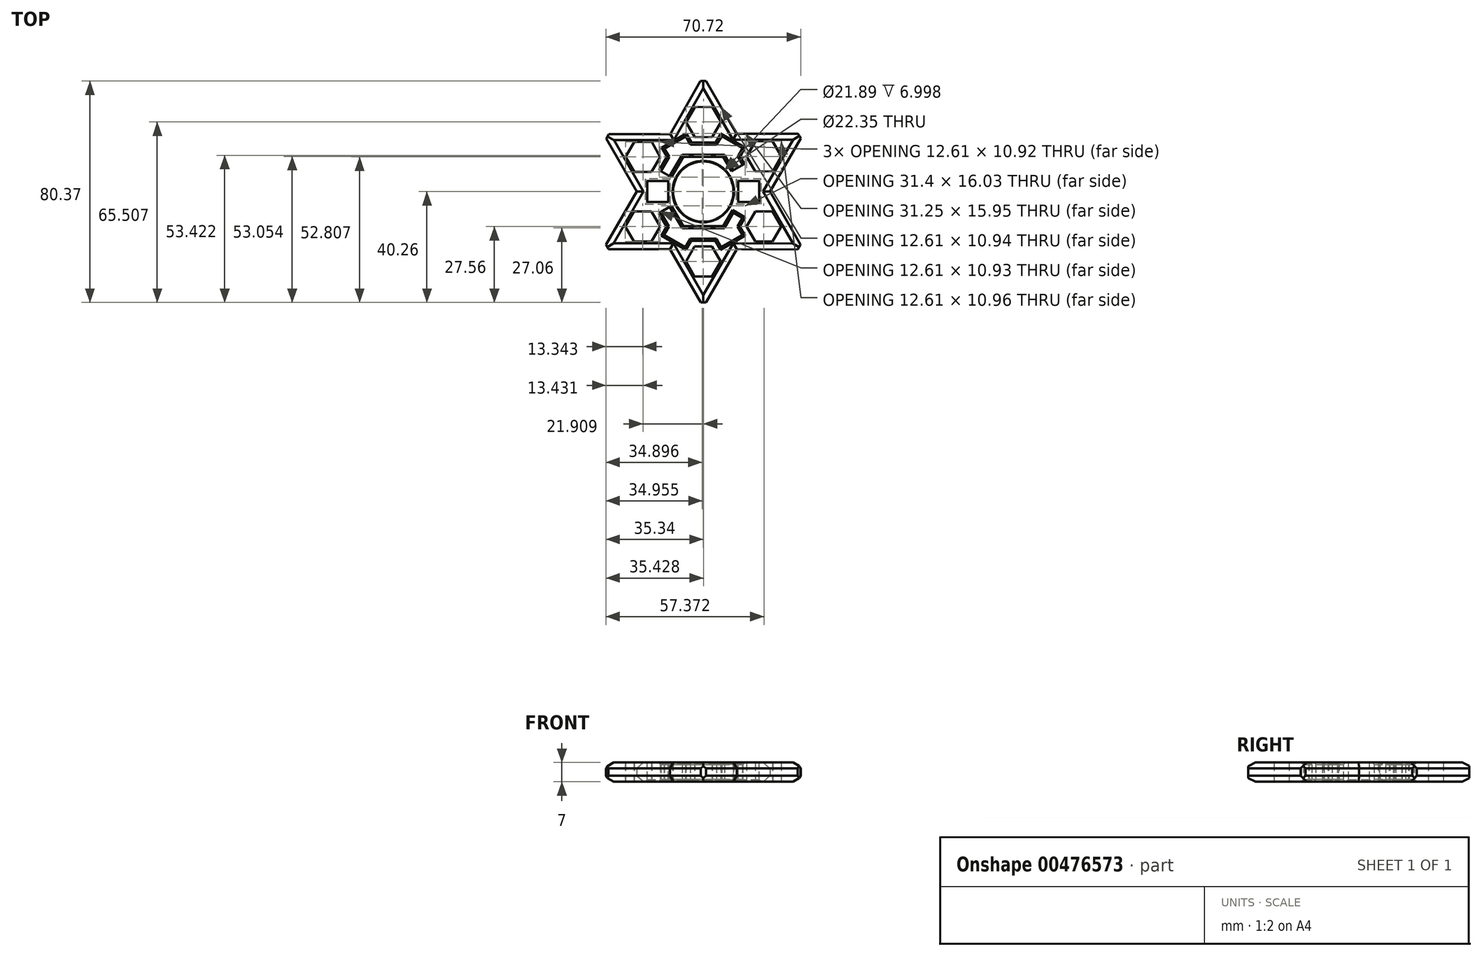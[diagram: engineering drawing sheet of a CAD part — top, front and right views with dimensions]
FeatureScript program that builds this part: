
annotation { "Feature Type Name" : "Feature", "Feature Type Description" : "" }
export const myFeature = defineFeature(function(context is Context, id is Id, definition is map)
    precondition{}
    {
        {
            var Q0;
            Q0=qCreatedBy(makeId("Top.planeOp"),FACE);
            var sketch = newSketch(context, id + "F0", { "sketchPlane" : qUnion([Q0])});
            skCircle(sketch, "E0", {"center": v(0, 0) * mm, "radius": 10.95 * mm});
            skCircle(sketch, "E1.cCircle", {"center": v(0, 0) * mm, "radius": 12.7 * mm, "construction": true});
            skLineSegment(sketch, "E1.0", {"start": v(-7.33, 12.7) * mm, "end": v(7.33, 12.7) * mm});
            skLineSegment(sketch, "E1.1", {"start": v(7.33, 12.7) * mm, "end": v(14.66, 0) * mm});
            skLineSegment(sketch, "E1.2", {"start": v(14.66, 0) * mm, "end": v(7.33, -12.7) * mm});
            skLineSegment(sketch, "E1.3", {"start": v(7.33, -12.7) * mm, "end": v(-7.33, -12.7) * mm});
            skLineSegment(sketch, "E1.4", {"start": v(-7.33, -12.7) * mm, "end": v(-14.66, 0) * mm});
            skLineSegment(sketch, "E1.5", {"start": v(-14.66, 0) * mm, "end": v(-7.33, 12.7) * mm});
            skPoint(sketch, "E1.0.midPoint", {"position": v(0, 12.7) * mm});
            skPoint(sketch, "E2.endSnap0", {"position": v(0, -12.7) * mm});
            skCircle(sketch, "E3.cCircle", {"center": v(0.09, 25.25) * mm, "radius": 5.46 * mm, "construction": true});
            skLineSegment(sketch, "E3.0", {"start": v(3.26, 19.8) * mm, "end": v(-3.05, 19.78) * mm});
            skLineSegment(sketch, "E3.1", {"start": v(-3.05, 19.78) * mm, "end": v(-6.22, 25.23) * mm});
            skLineSegment(sketch, "E3.2", {"start": v(-6.22, 25.23) * mm, "end": v(-3.08, 30.7) * mm});
            skLineSegment(sketch, "E3.3", {"start": v(-3.08, 30.7) * mm, "end": v(3.22, 30.72) * mm});
            skLineSegment(sketch, "E3.4", {"start": v(3.22, 30.72) * mm, "end": v(6.4, 25.27) * mm});
            skLineSegment(sketch, "E3.5", {"start": v(6.4, 25.27) * mm, "end": v(3.26, 19.8) * mm});
            skPoint(sketch, "E3.0.midPoint", {"position": v(0.1, 19.79) * mm});
            skCircle(sketch, "E4.cCircle", {"center": v(22.03, 12.8) * mm, "radius": 5.46 * mm, "construction": true});
            skLineSegment(sketch, "E4.0", {"start": v(18.92, 7.31) * mm, "end": v(15.73, 12.75) * mm});
            skLineSegment(sketch, "E4.1", {"start": v(15.73, 12.75) * mm, "end": v(18.84, 18.23) * mm});
            skLineSegment(sketch, "E4.2", {"start": v(18.84, 18.23) * mm, "end": v(25.15, 18.28) * mm});
            skLineSegment(sketch, "E4.3", {"start": v(25.15, 18.28) * mm, "end": v(28.34, 12.83) * mm});
            skLineSegment(sketch, "E4.4", {"start": v(28.34, 12.83) * mm, "end": v(25.22, 7.35) * mm});
            skLineSegment(sketch, "E4.5", {"start": v(25.22, 7.35) * mm, "end": v(18.92, 7.31) * mm});
            skPoint(sketch, "E4.0.midPoint", {"position": v(17.32, 10.03) * mm});
            skCircle(sketch, "E5.cCircle", {"center": v(22, -12.7) * mm, "radius": 5.46 * mm, "construction": true});
            skLineSegment(sketch, "E5.0", {"start": v(15.7, -12.7) * mm, "end": v(18.84, -7.24) * mm});
            skLineSegment(sketch, "E5.1", {"start": v(18.84, -7.24) * mm, "end": v(25.15, -7.24) * mm});
            skLineSegment(sketch, "E5.2", {"start": v(25.15, -7.24) * mm, "end": v(28.3, -12.7) * mm});
            skLineSegment(sketch, "E5.3", {"start": v(28.3, -12.7) * mm, "end": v(25.15, -18.16) * mm});
            skLineSegment(sketch, "E5.4", {"start": v(25.15, -18.16) * mm, "end": v(18.85, -18.16) * mm});
            skLineSegment(sketch, "E5.5", {"start": v(18.85, -18.16) * mm, "end": v(15.7, -12.7) * mm});
            skPoint(sketch, "E5.0.midPoint", {"position": v(17.27, -9.97) * mm});
            skCircle(sketch, "E6.cCircle", {"center": v(0, -25.4) * mm, "radius": 5.46 * mm, "construction": true});
            skLineSegment(sketch, "E6.0", {"start": v(-3.15, -19.94) * mm, "end": v(3.15, -19.94) * mm});
            skLineSegment(sketch, "E6.1", {"start": v(3.15, -19.94) * mm, "end": v(6.3, -25.4) * mm});
            skLineSegment(sketch, "E6.2", {"start": v(6.3, -25.4) * mm, "end": v(3.15, -30.86) * mm});
            skLineSegment(sketch, "E6.3", {"start": v(3.15, -30.86) * mm, "end": v(-3.15, -30.86) * mm});
            skLineSegment(sketch, "E6.4", {"start": v(-3.15, -30.86) * mm, "end": v(-6.3, -25.4) * mm});
            skLineSegment(sketch, "E6.5", {"start": v(-6.3, -25.4) * mm, "end": v(-3.15, -19.94) * mm});
            skPoint(sketch, "E6.0.midPoint", {"position": v(0, -19.94) * mm});
            skCircle(sketch, "E7.cCircle", {"center": v(-22, -12.7) * mm, "radius": 5.46 * mm, "construction": true});
            skLineSegment(sketch, "E7.0", {"start": v(-18.85, -7.24) * mm, "end": v(-15.7, -12.7) * mm});
            skLineSegment(sketch, "E7.1", {"start": v(-15.7, -12.7) * mm, "end": v(-18.84, -18.16) * mm});
            skLineSegment(sketch, "E7.2", {"start": v(-18.84, -18.16) * mm, "end": v(-25.15, -18.16) * mm});
            skLineSegment(sketch, "E7.3", {"start": v(-25.15, -18.16) * mm, "end": v(-28.3, -12.7) * mm});
            skLineSegment(sketch, "E7.4", {"start": v(-28.3, -12.7) * mm, "end": v(-25.15, -7.24) * mm});
            skLineSegment(sketch, "E7.5", {"start": v(-25.15, -7.24) * mm, "end": v(-18.85, -7.24) * mm});
            skPoint(sketch, "E7.0.midPoint", {"position": v(-17.27, -9.97) * mm});
            skCircle(sketch, "E8.cCircle", {"center": v(-21.9, 12.55) * mm, "radius": 5.46 * mm, "construction": true});
            skLineSegment(sketch, "E8.0", {"start": v(-15.6, 12.55) * mm, "end": v(-18.76, 7.09) * mm});
            skLineSegment(sketch, "E8.1", {"start": v(-18.76, 7.09) * mm, "end": v(-25.06, 7.09) * mm});
            skLineSegment(sketch, "E8.2", {"start": v(-25.06, 7.09) * mm, "end": v(-28.21, 12.55) * mm});
            skLineSegment(sketch, "E8.3", {"start": v(-28.21, 12.55) * mm, "end": v(-25.06, 18) * mm});
            skLineSegment(sketch, "E8.4", {"start": v(-25.06, 18) * mm, "end": v(-18.75, 18) * mm});
            skLineSegment(sketch, "E8.5", {"start": v(-18.75, 18) * mm, "end": v(-15.6, 12.55) * mm});
            skPoint(sketch, "E8.0.midPoint", {"position": v(-17.18, 9.82) * mm});
            skCircle(sketch, "E9.cCircle", {"center": v(-21.9, 12.55) * mm, "radius": 8.26 * mm, "construction": true});
            skLineSegment(sketch, "E9.0", {"start": v(-12.38, 12.55) * mm, "end": v(-17.14, 4.3) * mm});
            skLineSegment(sketch, "E9.1", {"start": v(-17.14, 4.3) * mm, "end": v(-26.67, 4.3) * mm});
            skLineSegment(sketch, "E9.2", {"start": v(-26.67, 4.3) * mm, "end": v(-31.44, 12.55) * mm});
            skLineSegment(sketch, "E9.3", {"start": v(-31.44, 12.55) * mm, "end": v(-26.67, 20.8) * mm});
            skLineSegment(sketch, "E9.4", {"start": v(-26.67, 20.8) * mm, "end": v(-17.14, 20.8) * mm});
            skLineSegment(sketch, "E9.5", {"start": v(-17.14, 20.8) * mm, "end": v(-12.38, 12.55) * mm});
            skPoint(sketch, "E9.0.midPoint", {"position": v(-14.76, 8.42) * mm});
            skCircle(sketch, "E10.cCircle", {"center": v(0.09, 25.25) * mm, "radius": 8.26 * mm, "construction": true});
            skLineSegment(sketch, "E10.0", {"start": v(4.85, 17) * mm, "end": v(-4.68, 17) * mm});
            skLineSegment(sketch, "E10.1", {"start": v(-4.68, 17) * mm, "end": v(-9.44, 25.25) * mm});
            skLineSegment(sketch, "E10.2", {"start": v(-9.44, 25.25) * mm, "end": v(-4.68, 33.5) * mm});
            skLineSegment(sketch, "E10.3", {"start": v(-4.68, 33.5) * mm, "end": v(4.85, 33.5) * mm});
            skLineSegment(sketch, "E10.4", {"start": v(4.85, 33.5) * mm, "end": v(9.62, 25.25) * mm});
            skLineSegment(sketch, "E10.5", {"start": v(9.62, 25.25) * mm, "end": v(4.85, 17) * mm});
            skPoint(sketch, "E10.0.midPoint", {"position": v(0.09, 17) * mm});
            skCircle(sketch, "E11.cCircle", {"center": v(22.03, 12.8) * mm, "radius": 8.26 * mm, "construction": true});
            skLineSegment(sketch, "E11.0", {"start": v(17.27, 4.54) * mm, "end": v(12.5, 12.8) * mm});
            skLineSegment(sketch, "E11.1", {"start": v(12.5, 12.8) * mm, "end": v(17.27, 21.05) * mm});
            skLineSegment(sketch, "E11.2", {"start": v(17.27, 21.05) * mm, "end": v(26.8, 21.05) * mm});
            skLineSegment(sketch, "E11.3", {"start": v(26.8, 21.05) * mm, "end": v(31.56, 12.8) * mm});
            skLineSegment(sketch, "E11.4", {"start": v(31.56, 12.8) * mm, "end": v(26.8, 4.54) * mm});
            skLineSegment(sketch, "E11.5", {"start": v(26.8, 4.54) * mm, "end": v(17.27, 4.54) * mm});
            skPoint(sketch, "E11.0.midPoint", {"position": v(14.88, 8.67) * mm});
            skCircle(sketch, "E12.cCircle", {"center": v(22, -12.7) * mm, "radius": 8.26 * mm, "construction": true});
            skLineSegment(sketch, "E12.0", {"start": v(12.46, -12.7) * mm, "end": v(17.23, -4.44) * mm});
            skLineSegment(sketch, "E12.1", {"start": v(17.23, -4.45) * mm, "end": v(26.76, -4.44) * mm});
            skLineSegment(sketch, "E12.2", {"start": v(26.76, -4.44) * mm, "end": v(31.53, -12.7) * mm});
            skLineSegment(sketch, "E12.3", {"start": v(31.53, -12.7) * mm, "end": v(26.76, -20.96) * mm});
            skLineSegment(sketch, "E12.4", {"start": v(26.76, -20.96) * mm, "end": v(17.23, -20.96) * mm});
            skLineSegment(sketch, "E12.5", {"start": v(17.23, -20.96) * mm, "end": v(12.46, -12.7) * mm});
            skPoint(sketch, "E12.0.midPoint", {"position": v(14.85, -8.57) * mm});
            skCircle(sketch, "E13.cCircle", {"center": v(0, -25.4) * mm, "radius": 8.26 * mm, "construction": true});
            skLineSegment(sketch, "E13.0", {"start": v(-4.77, -17.14) * mm, "end": v(4.77, -17.14) * mm});
            skLineSegment(sketch, "E13.1", {"start": v(4.77, -17.15) * mm, "end": v(9.53, -25.4) * mm});
            skLineSegment(sketch, "E13.2", {"start": v(9.53, -25.4) * mm, "end": v(4.77, -33.65) * mm});
            skLineSegment(sketch, "E13.3", {"start": v(4.77, -33.65) * mm, "end": v(-4.77, -33.66) * mm});
            skLineSegment(sketch, "E13.4", {"start": v(-4.77, -33.66) * mm, "end": v(-9.53, -25.4) * mm});
            skLineSegment(sketch, "E13.5", {"start": v(-9.53, -25.4) * mm, "end": v(-4.77, -17.15) * mm});
            skPoint(sketch, "E13.0.midPoint", {"position": v(0, -17.14) * mm});
            skCircle(sketch, "E14.cCircle", {"center": v(-22, -12.7) * mm, "radius": 8.26 * mm, "construction": true});
            skLineSegment(sketch, "E14.0", {"start": v(-17.23, -4.45) * mm, "end": v(-12.46, -12.7) * mm});
            skLineSegment(sketch, "E14.1", {"start": v(-12.46, -12.7) * mm, "end": v(-17.23, -20.96) * mm});
            skLineSegment(sketch, "E14.2", {"start": v(-17.23, -20.96) * mm, "end": v(-26.76, -20.96) * mm});
            skLineSegment(sketch, "E14.3", {"start": v(-26.76, -20.96) * mm, "end": v(-31.53, -12.7) * mm});
            skLineSegment(sketch, "E14.4", {"start": v(-31.53, -12.7) * mm, "end": v(-26.76, -4.45) * mm});
            skLineSegment(sketch, "E14.5", {"start": v(-26.76, -4.45) * mm, "end": v(-17.23, -4.45) * mm});
            skPoint(sketch, "E14.0.midPoint", {"position": v(-14.85, -8.57) * mm});
            skLineSegment(sketch, "E15", {"start": v(-6.43, 20.02) * mm, "end": v(-14.12, 15.57) * mm});
            skLineSegment(sketch, "E16", {"start": v(-14.21, 15.73) * mm, "end": v(-15.4, 17.77) * mm});
            skLineSegment(sketch, "E17", {"start": v(-15.4, 17.77) * mm, "end": v(-7.7, 22.22) * mm});
            skLineSegment(sketch, "E18", {"start": v(-23.27, 4.3) * mm, "end": v(-23.27, -4.45) * mm});
            skLineSegment(sketch, "E19", {"start": v(-23.27, -4.45) * mm, "end": v(-20.73, -4.45) * mm});
            skLineSegment(sketch, "E20", {"start": v(-20.73, -4.45) * mm, "end": v(-20.73, 4.3) * mm});
            skLineSegment(sketch, "E21", {"start": v(-15.48, -17.93) * mm, "end": v(-7.78, -22.37) * mm});
            skLineSegment(sketch, "E22", {"start": v(-7.78, -22.37) * mm, "end": v(-6.51, -20.17) * mm});
            skLineSegment(sketch, "E23", {"start": v(-6.51, -20.17) * mm, "end": v(-14.21, -15.73) * mm});
            skLineSegment(sketch, "E24", {"start": v(6.51, -20.17) * mm, "end": v(14.21, -15.73) * mm});
            skLineSegment(sketch, "E25", {"start": v(14.21, -15.73) * mm, "end": v(15.48, -17.93) * mm});
            skLineSegment(sketch, "E26", {"start": v(15.48, -17.93) * mm, "end": v(7.7, -22.42) * mm});
            skLineSegment(sketch, "E27", {"start": v(20.73, -4.45) * mm, "end": v(20.73, 4.54) * mm});
            skLineSegment(sketch, "E28", {"start": v(20.73, 4.54) * mm, "end": v(23.27, 4.54) * mm});
            skLineSegment(sketch, "E29", {"start": v(23.27, 4.54) * mm, "end": v(23.27, -4.54) * mm});
            skLineSegment(sketch, "E30", {"start": v(14.2, 15.74) * mm, "end": v(6.65, 20.1) * mm});
            skLineSegment(sketch, "E31", {"start": v(6.65, 20.1) * mm, "end": v(7.96, 22.37) * mm});
            skLineSegment(sketch, "E32", {"start": v(7.96, 22.37) * mm, "end": v(15.5, 18) * mm});
            skLineSegment(sketch, "E33.bottom", {"start": v(-1.27, -12.7) * mm, "end": v(1.27, -12.7) * mm});
            skLineSegment(sketch, "E33.top", {"start": v(-1.27, -17.14) * mm, "end": v(1.27, -17.14) * mm});
            skLineSegment(sketch, "E34.bottom", {"start": v(1.27, 12.7) * mm, "end": v(-1.27, 12.7) * mm});
            skLineSegment(sketch, "E34.top", {"start": v(1.27, 17) * mm, "end": v(-1.27, 17) * mm});
            skLineSegment(sketch, "E35", {"start": v(14.28, 9.71) * mm, "end": v(10.3, 7.42) * mm});
            skLineSegment(sketch, "E36", {"start": v(10.3, 7.42) * mm, "end": v(11.63, 5.25) * mm});
            skLineSegment(sketch, "E37", {"start": v(11.63, 5.25) * mm, "end": v(15.55, 7.51) * mm});
            skLineSegment(sketch, "E38", {"start": v(15.48, -7.47) * mm, "end": v(11.58, -5.22) * mm});
            skLineSegment(sketch, "E39", {"start": v(11.58, -5.22) * mm, "end": v(10.36, -7.45) * mm});
            skLineSegment(sketch, "E40", {"start": v(10.36, -7.45) * mm, "end": v(14.21, -9.67) * mm});
            skLineSegment(sketch, "E41", {"start": v(-10.36, -7.45) * mm, "end": v(-14.21, -9.67) * mm});
            skLineSegment(sketch, "E42", {"start": v(-14.21, -9.67) * mm, "end": v(-15.48, -7.47) * mm});
            skLineSegment(sketch, "E43", {"start": v(-15.48, -7.47) * mm, "end": v(-11.63, -5.25) * mm});
            skLineSegment(sketch, "E44", {"start": v(-11.63, 5.25) * mm, "end": v(-15.35, 7.4) * mm});
            skLineSegment(sketch, "E45", {"start": v(-15.35, 7.4) * mm, "end": v(-14.08, 9.6) * mm});
            skLineSegment(sketch, "E46", {"start": v(-14.08, 9.6) * mm, "end": v(-10.36, 7.45) * mm});
            skLineSegment(sketch, "E47", {"start": v(-11.63, 5.25) * mm, "end": v(-10.36, 7.45) * mm});
            skLineSegment(sketch, "E48", {"start": v(-14.08, 9.6) * mm, "end": v(-15.35, 7.4) * mm});
            skLineSegment(sketch, "E49", {"start": v(15.55, 7.51) * mm, "end": v(14.28, 9.71) * mm});
            skLineSegment(sketch, "E50", {"start": v(-11.63, -5.25) * mm, "end": v(-15.48, -7.47) * mm});
            skLineSegment(sketch, "E51", {"start": v(-15.48, -7.47) * mm, "end": v(-14.21, -9.67) * mm});
            skLineSegment(sketch, "E52", {"start": v(-14.21, -9.67) * mm, "end": v(-10.36, -7.45) * mm});
            skLineSegment(sketch, "E53", {"start": v(-10.36, -7.45) * mm, "end": v(-11.63, -5.25) * mm});
            skCircle(sketch, "E54", {"center": v(0, 0) * mm, "radius": 11.08 * mm});
            skCircle(sketch, "E55", {"center": v(0, 0) * mm, "radius": 11.07 * mm});
            skLineSegment(sketch, "E56", {"start": v(9.62, 25.25) * mm, "end": v(0, 41.9) * mm});
            skLineSegment(sketch, "E57", {"start": v(0, 41.9) * mm, "end": v(-9.44, 25.25) * mm});
            skLineSegment(sketch, "E58", {"start": v(-17.14, 20.8) * mm, "end": v(-35.5, 20.8) * mm});
            skLineSegment(sketch, "E59", {"start": v(-26.67, 4.3) * mm, "end": v(-36.2, 20.8) * mm});
            skLineSegment(sketch, "E60", {"start": v(-36.2, 20.8) * mm, "end": v(-35.5, 20.8) * mm});
            skLineSegment(sketch, "E61", {"start": v(26.8, 4.54) * mm, "end": v(36.33, 21.05) * mm});
            skLineSegment(sketch, "E62", {"start": v(36.33, 21.05) * mm, "end": v(17.27, 21.05) * mm});
            skLineSegment(sketch, "E63", {"start": v(26.76, -4.44) * mm, "end": v(36.38, -21.1) * mm});
            skLineSegment(sketch, "E64", {"start": v(36.38, -21.1) * mm, "end": v(17.23, -20.96) * mm});
            skLineSegment(sketch, "E65", {"start": v(9.53, -25.4) * mm, "end": v(0, -41.91) * mm});
            skLineSegment(sketch, "E66", {"start": v(0, -41.91) * mm, "end": v(-9.53, -25.4) * mm});
            skLineSegment(sketch, "E67", {"start": v(-26.76, -4.45) * mm, "end": v(-36.3, -20.96) * mm});
            skLineSegment(sketch, "E68", {"start": v(-36.3, -20.96) * mm, "end": v(-17.23, -20.96) * mm});
            skLineSegment(sketch, "E69", {"start": v(-29.06, 16.67) * mm, "end": v(-36.2, 20.8) * mm});
            skLineSegment(sketch, "E70", {"start": v(-35.25, 19.15) * mm, "end": v(-34.3, 20.8) * mm});
            skLineSegment(sketch, "E71", {"start": v(-1.02, 40.1) * mm, "end": v(1.04, 40.1) * mm});
            skLineSegment(sketch, "E72", {"start": v(34.42, 21.05) * mm, "end": v(35.38, 19.4) * mm});
            skLineSegment(sketch, "E73", {"start": v(35.34, -19.3) * mm, "end": v(34.31, -21.09) * mm});
            skLineSegment(sketch, "E74", {"start": v(0.95, -40.26) * mm, "end": v(-0.95, -40.26) * mm});
            skLineSegment(sketch, "E75", {"start": v(-34.39, -20.96) * mm, "end": v(-35.34, -19.3) * mm});
            skLineSegment(sketch, "E76", {"start": v(-26.76, -4.45) * mm, "end": v(-24.2, 0) * mm});
            skLineSegment(sketch, "E77", {"start": v(-24.2, 0) * mm, "end": v(-26.67, 4.3) * mm});
            skLineSegment(sketch, "E78", {"start": v(-17.14, 20.8) * mm, "end": v(-10.15, 20.8) * mm});
            skLineSegment(sketch, "E79", {"start": v(-9.44, 25.25) * mm, "end": v(-11.96, 20.8) * mm});
            skLineSegment(sketch, "E80", {"start": v(9.62, 25.25) * mm, "end": v(12.03, 21.08) * mm});
            skLineSegment(sketch, "E81", {"start": v(17.27, 21.05) * mm, "end": v(10.24, 21.05) * mm});
            skLineSegment(sketch, "E82", {"start": v(26.8, 4.54) * mm, "end": v(24.18, 0) * mm});
            skLineSegment(sketch, "E83", {"start": v(24.18, 0) * mm, "end": v(26.76, -4.45) * mm});
            skLineSegment(sketch, "E84", {"start": v(17.23, -20.96) * mm, "end": v(11.12, -20.9) * mm});
            skLineSegment(sketch, "E85", {"start": v(9.53, -25.4) * mm, "end": v(12.12, -20.92) * mm});
            skLineSegment(sketch, "E86", {"start": v(-9.53, -25.4) * mm, "end": v(-12.47, -20.32) * mm});
            skLineSegment(sketch, "E87", {"start": v(-17.23, -20.96) * mm, "end": v(-12.1, -20.96) * mm});
            skCircle(sketch, "E88", {"center": v(0, 0) * mm, "radius": 10.94 * mm});
            skLineSegment(sketch, "E89", {"start": v(9.62, 25.25) * mm, "end": v(12.23, 20.73) * mm});
            skSolve(sketch);
        }
        {
            var Q0;
            {var subQ1=sQuery(id+"F0.wireOp",EDGE,"E11.2");Q0=makeQuery(id+"F0.imprint","IMPRINT",FACE,{"disambiguationData":[TD([[makeQuery(id+"F0.imprint","IMPRINT",EDGE,{"derivedFrom":subQ1}),1.0]])]});}
            var Q1;
            {var subQ4=sQuery(id+"F0.wireOp",EDGE,"E12.3");Q1=makeQuery(id+"F0.imprint","IMPRINT",FACE,{"disambiguationData":[TD([[makeQuery(id+"F0.imprint","IMPRINT",EDGE,{"derivedFrom":subQ4}),1.0]])]});}
            var Q2;
            {var subQ0=sQuery(id+"F0.wireOp",EDGE,"E13.3");Q2=makeQuery(id+"F0.imprint","IMPRINT",FACE,{"disambiguationData":[TD([[makeQuery(id+"F0.imprint","IMPRINT",EDGE,{"derivedFrom":subQ0}),1.0]])]});}
            var Q3;
            {var subQ3=sQuery(id+"F0.wireOp",EDGE,"E14.2");Q3=makeQuery(id+"F0.imprint","IMPRINT",FACE,{"disambiguationData":[TD([[makeQuery(id+"F0.imprint","IMPRINT",EDGE,{"derivedFrom":subQ3}),1.0]])]});}
            var Q4;
            {var subQ0=sQuery(id+"F0.wireOp",EDGE,"E18");Q4=makeQuery(id+"F0.imprint","IMPRINT",FACE,{"disambiguationData":[TD([[makeQuery(id+"F0.imprint","IMPRINT",EDGE,{"derivedFrom":subQ0}),1.0]])]});}
            var Q5;
            {var subQ0=sQuery(id+"F0.wireOp",EDGE,"E59");var subQ1=sQuery(id+"F0.wireOp",EDGE,"E9.3");var subQ2=makeQuery(id+"F0.imprint","INTERSECT",VERTEX,{"derivedFrom":[subQ1,subQ0]});Q5=makeQuery(id+"F0.imprint","IMPRINT",FACE,{"disambiguationData":[TD([[makeQuery(id+"F0.imprint","IMPRINT",EDGE,{"disambiguationData":[TD([[subQ2,-1.0]])],"derivedFrom":subQ1}),1.0]])]});}
            var Q6;
            {var subQ0=sQuery(id+"F0.wireOp",EDGE,"E58");var subQ1=sQuery(id+"F0.wireOp",EDGE,"E9.3");var subQ2=makeQuery(id+"F0.imprint","INTERSECT",VERTEX,{"derivedFrom":[subQ1,subQ0]});Q6=makeQuery(id+"F0.imprint","IMPRINT",FACE,{"disambiguationData":[TD([[makeQuery(id+"F0.imprint","IMPRINT",EDGE,{"disambiguationData":[TD([[subQ2,1.0]])],"derivedFrom":subQ1}),1.0]])]});}
            var Q7;
            {var subQ1=sQuery(id+"F0.wireOp",EDGE,"E15");Q7=makeQuery(id+"F0.imprint","IMPRINT",FACE,{"disambiguationData":[TD([[makeQuery(id+"F0.imprint","IMPRINT",EDGE,{"derivedFrom":subQ1}),-1.0]])]});}
            var Q8;
            {var subQ0=sQuery(id+"F0.wireOp",EDGE,"E30");Q8=makeQuery(id+"F0.imprint","IMPRINT",FACE,{"disambiguationData":[TD([[makeQuery(id+"F0.imprint","IMPRINT",EDGE,{"derivedFrom":subQ0}),-1.0]])]});}
            var Q9;
            {var subQ0=sQuery(id+"F0.wireOp",EDGE,"E27");Q9=makeQuery(id+"F0.imprint","IMPRINT",FACE,{"disambiguationData":[TD([[makeQuery(id+"F0.imprint","IMPRINT",EDGE,{"derivedFrom":subQ0}),-1.0]])]});}
            var Q10;
            {var subQ0=sQuery(id+"F0.wireOp",EDGE,"E24");Q10=makeQuery(id+"F0.imprint","IMPRINT",FACE,{"disambiguationData":[TD([[makeQuery(id+"F0.imprint","IMPRINT",EDGE,{"derivedFrom":subQ0}),-1.0]])]});}
            var Q11;
            {var subQ0=sQuery(id+"F0.wireOp",EDGE,"E21");Q11=makeQuery(id+"F0.imprint","IMPRINT",FACE,{"disambiguationData":[TD([[makeQuery(id+"F0.imprint","IMPRINT",EDGE,{"derivedFrom":subQ0}),1.0]])]});}
            var Q12;
            Q12=makeQuery(id+"F0.imprint","IMPRINT",FACE,{"disambiguationData":[TD([[makeQuery(id+"F0.imprint","IMPRINT",EDGE,{"derivedFrom":sQuery(id+"F0.wireOp",EDGE,"E3.0")}),1.0]])]});
            var Q13;
            Q13=makeQuery(id+"F0.imprint","IMPRINT",FACE,{"disambiguationData":[TD([[makeQuery(id+"F0.imprint","IMPRINT",EDGE,{"derivedFrom":sQuery(id+"F0.wireOp",EDGE,"E6.0")}),1.0]])]});
            var Q14;
            Q14=makeQuery(id+"F0.imprint","IMPRINT",FACE,{"disambiguationData":[TD([[makeQuery(id+"F0.imprint","IMPRINT",EDGE,{"derivedFrom":sQuery(id+"F0.wireOp",EDGE,"E4.0")}),1.0]])]});
            var Q15;
            Q15=makeQuery(id+"F0.imprint","IMPRINT",FACE,{"disambiguationData":[TD([[makeQuery(id+"F0.imprint","IMPRINT",EDGE,{"derivedFrom":sQuery(id+"F0.wireOp",EDGE,"E5.0")}),1.0]])]});
            var Q16;
            Q16=makeQuery(id+"F0.imprint","IMPRINT",FACE,{"disambiguationData":[TD([[makeQuery(id+"F0.imprint","IMPRINT",EDGE,{"derivedFrom":sQuery(id+"F0.wireOp",EDGE,"E7.0")}),1.0]])]});
            var Q17;
            Q17=makeQuery(id+"F0.imprint","IMPRINT",FACE,{"disambiguationData":[TD([[makeQuery(id+"F0.imprint","IMPRINT",EDGE,{"derivedFrom":sQuery(id+"F0.wireOp",EDGE,"E8.0")}),1.0]])]});
            var Q18;
            {var subQ0=sQuery(id+"F0.wireOp",EDGE,"E50");Q18=makeQuery(id+"F0.imprint","IMPRINT",FACE,{"disambiguationData":[TD([[makeQuery(id+"F0.imprint","IMPRINT",EDGE,{"derivedFrom":subQ0}),1.0]])]});}
            var Q19;
            {var subQ3=sQuery(id+"F0.wireOp",EDGE,"E40");Q19=makeQuery(id+"F0.imprint","IMPRINT",FACE,{"disambiguationData":[TD([[makeQuery(id+"F0.imprint","IMPRINT",EDGE,{"derivedFrom":subQ3}),1.0]])]});}
            var Q20;
            {var subQ4=sQuery(id+"F0.wireOp",EDGE,"E37");Q20=makeQuery(id+"F0.imprint","IMPRINT",FACE,{"disambiguationData":[TD([[makeQuery(id+"F0.imprint","IMPRINT",EDGE,{"derivedFrom":subQ4}),1.0]])]});}
            var Q21;
            {var subQ0=sQuery(id+"F0.wireOp",EDGE,"E46");Q21=makeQuery(id+"F0.imprint","IMPRINT",FACE,{"disambiguationData":[TD([[makeQuery(id+"F0.imprint","IMPRINT",EDGE,{"derivedFrom":subQ0}),-1.0]])]});}
            var Q22;
            {var subQ0=sQuery(id+"F0.wireOp",EDGE,"E14.3");Q22=makeQuery(id+"F0.imprint","IMPRINT",FACE,{"disambiguationData":[TD([[makeQuery(id+"F0.imprint","IMPRINT",EDGE,{"derivedFrom":subQ0}),1.0]])]});}
            var Q23;
            {var subQ0=sQuery(id+"F0.wireOp",EDGE,"E18");Q23=makeQuery(id+"F0.imprint","IMPRINT",FACE,{"disambiguationData":[TD([[makeQuery(id+"F0.imprint","IMPRINT",EDGE,{"derivedFrom":subQ0}),-1.0]])]});}
            var Q24;
            {var subQ0=sQuery(id+"F0.wireOp",EDGE,"E78");var subQ3=sQuery(id+"F0.wireOp",EDGE,"E17");var subQ5=makeQuery(id+"F0.imprint","INTERSECT",VERTEX,{"derivedFrom":[subQ3,subQ0]});Q24=makeQuery(id+"F0.imprint","IMPRINT",FACE,{"disambiguationData":[TD([[makeQuery(id+"F0.imprint","IMPRINT",EDGE,{"disambiguationData":[TD([[subQ5,1.0]])],"derivedFrom":subQ0}),-1.0]])]});}
            var Q25;
            {var subQ0=sQuery(id+"F0.wireOp",EDGE,"E79");Q25=makeQuery(id+"F0.imprint","IMPRINT",FACE,{"disambiguationData":[TD([[makeQuery(id+"F0.imprint","IMPRINT",EDGE,{"derivedFrom":subQ0}),1.0]])]});}
            var Q26;
            {var subQ0=sQuery(id+"F0.wireOp",EDGE,"E81");Q26=makeQuery(id+"F0.imprint","IMPRINT",FACE,{"disambiguationData":[TD([[makeQuery(id+"F0.imprint","IMPRINT",EDGE,{"derivedFrom":subQ0}),1.0]])]});}
            var Q27;
            {var subQ0=sQuery(id+"F0.wireOp",EDGE,"E82");Q27=makeQuery(id+"F0.imprint","IMPRINT",FACE,{"disambiguationData":[TD([[makeQuery(id+"F0.imprint","IMPRINT",EDGE,{"derivedFrom":subQ0}),-1.0]])]});}
            var Q28;
            {var subQ0=sQuery(id+"F0.wireOp",EDGE,"E21");Q28=makeQuery(id+"F0.imprint","IMPRINT",FACE,{"disambiguationData":[TD([[makeQuery(id+"F0.imprint","IMPRINT",EDGE,{"derivedFrom":subQ0}),-1.0]])]});}
            var Q29;
            {var subQ3=sQuery(id+"F0.wireOp",EDGE,"E85");Q29=makeQuery(id+"F0.imprint","IMPRINT",FACE,{"disambiguationData":[TD([[makeQuery(id+"F0.imprint","IMPRINT",EDGE,{"derivedFrom":subQ3}),1.0]])]});}
            var Q30;
            Q30=makeQuery(id+"F0.imprint","IMPRINT",FACE,{"disambiguationData":[TD([[makeQuery(id+"F0.imprint","IMPRINT",EDGE,{"derivedFrom":sQuery(id+"F0.wireOp",EDGE,"E0")}),-1.0]])]});
            var Q31;
            {var subQ3=sQuery(id+"F0.wireOp",EDGE,"E20");Q31=makeQuery(id+"F0.imprint","IMPRINT",FACE,{"disambiguationData":[TD([[makeQuery(id+"F0.imprint","IMPRINT",EDGE,{"derivedFrom":subQ3}),-1.0]])]});}
            var Q32;
            {var subQ3=sQuery(id+"F0.wireOp",EDGE,"E27");Q32=makeQuery(id+"F0.imprint","IMPRINT",FACE,{"disambiguationData":[TD([[makeQuery(id+"F0.imprint","IMPRINT",EDGE,{"derivedFrom":subQ3}),1.0]])]});}
            var Q33;
            {var subQ1=sQuery(id+"F0.wireOp",EDGE,"E10.2");Q33=makeQuery(id+"F0.imprint","IMPRINT",FACE,{"disambiguationData":[TD([[makeQuery(id+"F0.imprint","IMPRINT",EDGE,{"derivedFrom":subQ1}),1.0]])]});}
            var Q34;
            {var subQ3=sQuery(id+"F0.wireOp",EDGE,"E32");var subQ5=sQuery(id+"F0.wireOp",EDGE,"E81");var subQ6=makeQuery(id+"F0.imprint","INTERSECT",VERTEX,{"derivedFrom":[subQ3,subQ5]});Q34=makeQuery(id+"F0.imprint","IMPRINT",FACE,{"disambiguationData":[TD([[makeQuery(id+"F0.imprint","IMPRINT",EDGE,{"disambiguationData":[TD([[subQ6,1.0]])],"derivedFrom":subQ5}),-1.0]])]});}
            var Q35;
            {var subQ0=sQuery(id+"F0.wireOp",EDGE,"E11.3");Q35=makeQuery(id+"F0.imprint","IMPRINT",FACE,{"disambiguationData":[TD([[makeQuery(id+"F0.imprint","IMPRINT",EDGE,{"derivedFrom":subQ0}),1.0]])]});}
            extrude(context, id + "F1", {"entities" : qUnion([Q0, Q1, Q2, Q3, Q4, Q5, Q6, Q7, Q8, Q9, Q10, Q11, Q12, Q13, Q14, Q15, Q16, Q17, Q18, Q19, Q20, Q21, Q22, Q23, Q24, Q25, Q26, Q27, Q28, Q29, Q30, Q31, Q32, Q33, Q34, Q35]), "depth" : 7 * mm, "offsetDistance" : 25.4 * mm});
        }
        {
            var Q0;
            Q0=qCreatedBy(makeId("Top.planeOp"),FACE);
            var sketch = newSketch(context, id + "F2", { "sketchPlane" : qUnion([Q0])});
            skCircle(sketch, "E90", {"center": v(0, 0) * mm, "radius": 11.18 * mm});
            skCircle(sketch, "E91.cCircle", {"center": v(0, 0) * mm, "radius": 13.34 * mm, "construction": true});
            skLineSegment(sketch, "E91.0", {"start": v(-7.7, 13.33) * mm, "end": v(7.7, 13.34) * mm});
            skLineSegment(sketch, "E91.1", {"start": v(7.7, 13.34) * mm, "end": v(15.4, 0) * mm});
            skLineSegment(sketch, "E91.2", {"start": v(15.4, 0) * mm, "end": v(7.7, -13.33) * mm});
            skLineSegment(sketch, "E91.3", {"start": v(7.7, -13.33) * mm, "end": v(-7.7, -13.34) * mm});
            skLineSegment(sketch, "E91.4", {"start": v(-7.7, -13.34) * mm, "end": v(-15.4, 0) * mm});
            skLineSegment(sketch, "E91.5", {"start": v(-15.4, 0) * mm, "end": v(-7.7, 13.33) * mm});
            skPoint(sketch, "E91.0.midPoint", {"position": v(0, 13.33) * mm});
            skSolve(sketch);
        }
        {
            var Q0;
            Q0=makeQuery(id+"F2.imprint","IMPRINT",FACE,{"disambiguationData":[TD([[makeQuery(id+"F2.imprint","IMPRINT",EDGE,{"derivedFrom":sQuery(id+"F2.wireOp",EDGE,"E90")}),-1.0]])]});
            extrude(context, id + "F3", {"entities" : qUnion([Q0]), "operationType" : NewBodyOperationType.ADD, "depth" : 7 * mm, "offsetDistance" : 25.4 * mm});
        }
        {
            var Q0;
            Q0=makeQuery(id+"F1.opExtrude","CAP_EDGE",EDGE,{"disambiguationData":[OSD([sQuery(id+"F0.wireOp",EDGE,"E59"),sQuery(id+"F0.wireOp",EDGE,"E77")])],"isStart":true});
            var Q1;
            Q1=makeQuery(id+"F1.opExtrude","CAP_EDGE",EDGE,{"disambiguationData":[OSD([sQuery(id+"F0.wireOp",EDGE,"E59"),sQuery(id+"F0.wireOp",EDGE,"E77")])],"isStart":false});
            var Q2;
            Q2=makeQuery(id+"F1.opExtrude","CAP_EDGE",EDGE,{"disambiguationData":[OSD([sQuery(id+"F0.wireOp",EDGE,"E58"),sQuery(id+"F0.wireOp",EDGE,"E60"),sQuery(id+"F0.wireOp",EDGE,"E78")])],"isStart":true});
            var Q3;
            Q3=makeQuery(id+"F1.opExtrude","CAP_EDGE",EDGE,{"disambiguationData":[OSD([sQuery(id+"F0.wireOp",EDGE,"E58"),sQuery(id+"F0.wireOp",EDGE,"E60"),sQuery(id+"F0.wireOp",EDGE,"E78")])],"isStart":false});
            var Q4;
            Q4=makeQuery(id+"F1.opExtrude","CAP_EDGE",EDGE,{"disambiguationData":[OSD([sQuery(id+"F0.wireOp",EDGE,"E67"),sQuery(id+"F0.wireOp",EDGE,"E76")])],"isStart":false});
            var Q5;
            Q5=makeQuery(id+"F1.opExtrude","CAP_EDGE",EDGE,{"disambiguationData":[OSD([sQuery(id+"F0.wireOp",EDGE,"E57"),sQuery(id+"F0.wireOp",EDGE,"E79")])],"isStart":true});
            var Q6;
            Q6=makeQuery(id+"F1.opExtrude","CAP_EDGE",EDGE,{"disambiguationData":[OSD([sQuery(id+"F0.wireOp",EDGE,"E57"),sQuery(id+"F0.wireOp",EDGE,"E79")])],"isStart":false});
            var Q7;
            Q7=makeQuery(id+"F1.opExtrude","CAP_EDGE",EDGE,{"disambiguationData":[OSD([sQuery(id+"F0.wireOp",EDGE,"E67"),sQuery(id+"F0.wireOp",EDGE,"E76")])],"isStart":true});
            var Q8;
            Q8=makeQuery(id+"F1.opExtrude","CAP_EDGE",EDGE,{"disambiguationData":[OSD([sQuery(id+"F0.wireOp",EDGE,"E63")])],"isStart":true});
            var Q9;
            Q9=makeQuery(id+"F1.opExtrude","CAP_EDGE",EDGE,{"disambiguationData":[OSD([sQuery(id+"F0.wireOp",EDGE,"E63")])],"isStart":false});
            var Q10;
            Q10=makeQuery(id+"F1.opExtrude","CAP_EDGE",EDGE,{"disambiguationData":[OSD([sQuery(id+"F0.wireOp",EDGE,"E61"),sQuery(id+"F0.wireOp",EDGE,"E82")])],"isStart":true});
            var Q11;
            Q11=makeQuery(id+"F1.opExtrude","CAP_EDGE",EDGE,{"disambiguationData":[OSD([sQuery(id+"F0.wireOp",EDGE,"E61"),sQuery(id+"F0.wireOp",EDGE,"E82")])],"isStart":false});
            var Q12;
            Q12=makeQuery(id+"F1.opExtrude","CAP_EDGE",EDGE,{"disambiguationData":[OSD([sQuery(id+"F0.wireOp",EDGE,"E83")])],"isStart":true});
            var Q13;
            Q13=makeQuery(id+"F1.opExtrude","CAP_EDGE",EDGE,{"disambiguationData":[OSD([sQuery(id+"F0.wireOp",EDGE,"E83")])],"isStart":false});
            var Q14;
            Q14=makeQuery(id+"F1.opExtrude","CAP_EDGE",EDGE,{"disambiguationData":[OSD([sQuery(id+"F0.wireOp",EDGE,"E62"),sQuery(id+"F0.wireOp",EDGE,"E81")])],"isStart":true});
            var Q15;
            Q15=makeQuery(id+"F1.opExtrude","CAP_EDGE",EDGE,{"disambiguationData":[OSD([sQuery(id+"F0.wireOp",EDGE,"E62"),sQuery(id+"F0.wireOp",EDGE,"E81")])],"isStart":false});
            var Q16;
            Q16=makeQuery(id+"F1.opExtrude","CAP_EDGE",EDGE,{"disambiguationData":[OSD([sQuery(id+"F0.wireOp",EDGE,"E56"),sQuery(id+"F0.wireOp",EDGE,"E89")])],"isStart":true});
            var Q17;
            Q17=makeQuery(id+"F1.opExtrude","CAP_EDGE",EDGE,{"disambiguationData":[OSD([sQuery(id+"F0.wireOp",EDGE,"E56"),sQuery(id+"F0.wireOp",EDGE,"E89")])],"isStart":false});
            var Q18;
            Q18=makeQuery(id+"F1.opExtrude","CAP_EDGE",EDGE,{"disambiguationData":[OSD([sQuery(id+"F0.wireOp",EDGE,"E64"),sQuery(id+"F0.wireOp",EDGE,"E84")])],"isStart":true});
            var Q19;
            Q19=makeQuery(id+"F1.opExtrude","CAP_EDGE",EDGE,{"disambiguationData":[OSD([sQuery(id+"F0.wireOp",EDGE,"E65"),sQuery(id+"F0.wireOp",EDGE,"E85")])],"isStart":true});
            var Q20;
            Q20=makeQuery(id+"F1.opExtrude","CAP_EDGE",EDGE,{"disambiguationData":[OSD([sQuery(id+"F0.wireOp",EDGE,"E65"),sQuery(id+"F0.wireOp",EDGE,"E85")])],"isStart":false});
            var Q21;
            Q21=makeQuery(id+"F1.opExtrude","CAP_EDGE",EDGE,{"disambiguationData":[OSD([sQuery(id+"F0.wireOp",EDGE,"E64"),sQuery(id+"F0.wireOp",EDGE,"E84")])],"isStart":false});
            var Q22;
            Q22=makeQuery(id+"F1.opExtrude","CAP_EDGE",EDGE,{"disambiguationData":[OSD([sQuery(id+"F0.wireOp",EDGE,"E68"),sQuery(id+"F0.wireOp",EDGE,"E87")])],"isStart":true});
            var Q23;
            Q23=makeQuery(id+"F1.opExtrude","CAP_EDGE",EDGE,{"disambiguationData":[OSD([sQuery(id+"F0.wireOp",EDGE,"E68"),sQuery(id+"F0.wireOp",EDGE,"E87")])],"isStart":false});
            var Q24;
            Q24=makeQuery(id+"F1.opExtrude","CAP_EDGE",EDGE,{"disambiguationData":[OSD([sQuery(id+"F0.wireOp",EDGE,"E66"),sQuery(id+"F0.wireOp",EDGE,"E86")])],"isStart":true});
            var Q25;
            Q25=makeQuery(id+"F1.opExtrude","CAP_EDGE",EDGE,{"disambiguationData":[OSD([sQuery(id+"F0.wireOp",EDGE,"E66"),sQuery(id+"F0.wireOp",EDGE,"E86")])],"isStart":false});
            chamfer(context, id + "F4", {"entities" : qUnion([Q0, Q1, Q2, Q3, Q4, Q5, Q6, Q7, Q8, Q9, Q10, Q11, Q12, Q13, Q14, Q15, Q16, Q17, Q18, Q19, Q20, Q21, Q22, Q23, Q24, Q25]), "width" : 2.16 * mm, "tangentPropagation" : true});
        }
        {
            var Q0;
            Q0=makeQuery(id+"F3.boolean.opBoolean","MERGE",FACE,{"derivedFrom":[makeQuery(id+"F1.opExtrude","CAP_FACE",FACE,{"disambiguationData":[OSD([sQuery(id+"F0.wireOp",EDGE,"E3.0"),sQuery(id+"F0.wireOp",EDGE,"E3.1"),sQuery(id+"F0.wireOp",EDGE,"E3.2"),sQuery(id+"F0.wireOp",EDGE,"E3.3"),sQuery(id+"F0.wireOp",EDGE,"E3.4"),sQuery(id+"F0.wireOp",EDGE,"E3.5"),sQuery(id+"F0.wireOp",EDGE,"E4.0"),sQuery(id+"F0.wireOp",EDGE,"E4.1"),sQuery(id+"F0.wireOp",EDGE,"E4.2"),sQuery(id+"F0.wireOp",EDGE,"E4.3"),sQuery(id+"F0.wireOp",EDGE,"E4.4"),sQuery(id+"F0.wireOp",EDGE,"E4.5"),sQuery(id+"F0.wireOp",EDGE,"E5.0"),sQuery(id+"F0.wireOp",EDGE,"E5.1"),sQuery(id+"F0.wireOp",EDGE,"E5.2"),sQuery(id+"F0.wireOp",EDGE,"E5.3"),sQuery(id+"F0.wireOp",EDGE,"E5.4"),sQuery(id+"F0.wireOp",EDGE,"E5.5"),sQuery(id+"F0.wireOp",EDGE,"E6.0"),sQuery(id+"F0.wireOp",EDGE,"E6.1"),sQuery(id+"F0.wireOp",EDGE,"E6.2"),sQuery(id+"F0.wireOp",EDGE,"E6.3"),sQuery(id+"F0.wireOp",EDGE,"E6.4"),sQuery(id+"F0.wireOp",EDGE,"E6.5"),sQuery(id+"F0.wireOp",EDGE,"E7.0"),sQuery(id+"F0.wireOp",EDGE,"E7.1"),sQuery(id+"F0.wireOp",EDGE,"E7.2"),sQuery(id+"F0.wireOp",EDGE,"E7.3"),sQuery(id+"F0.wireOp",EDGE,"E7.4"),sQuery(id+"F0.wireOp",EDGE,"E7.5"),sQuery(id+"F0.wireOp",EDGE,"E8.0"),sQuery(id+"F0.wireOp",EDGE,"E8.1"),sQuery(id+"F0.wireOp",EDGE,"E8.2"),sQuery(id+"F0.wireOp",EDGE,"E8.3"),sQuery(id+"F0.wireOp",EDGE,"E8.4"),sQuery(id+"F0.wireOp",EDGE,"E8.5"),sQuery(id+"F0.wireOp",EDGE,"E9.0"),sQuery(id+"F0.wireOp",EDGE,"E9.1"),sQuery(id+"F0.wireOp",EDGE,"E9.5"),sQuery(id+"F0.wireOp",EDGE,"E10.0"),sQuery(id+"F0.wireOp",EDGE,"E10.1"),sQuery(id+"F0.wireOp",EDGE,"E10.5"),sQuery(id+"F0.wireOp",EDGE,"E11.0"),sQuery(id+"F0.wireOp",EDGE,"E11.1"),sQuery(id+"F0.wireOp",EDGE,"E11.5"),sQuery(id+"F0.wireOp",EDGE,"E12.0"),sQuery(id+"F0.wireOp",EDGE,"E12.1"),sQuery(id+"F0.wireOp",EDGE,"E12.5"),sQuery(id+"F0.wireOp",EDGE,"E13.0"),sQuery(id+"F0.wireOp",EDGE,"E13.1"),sQuery(id+"F0.wireOp",EDGE,"E13.5"),sQuery(id+"F0.wireOp",EDGE,"E14.0"),sQuery(id+"F0.wireOp",EDGE,"E14.1"),sQuery(id+"F0.wireOp",EDGE,"E14.2"),sQuery(id+"F0.wireOp",EDGE,"E14.3"),sQuery(id+"F0.wireOp",EDGE,"E14.5"),sQuery(id+"F0.wireOp",EDGE,"E15"),sQuery(id+"F0.wireOp",EDGE,"E17"),sQuery(id+"F0.wireOp",EDGE,"E18"),sQuery(id+"F0.wireOp",EDGE,"E21"),sQuery(id+"F0.wireOp",EDGE,"E23"),sQuery(id+"F0.wireOp",EDGE,"E24"),sQuery(id+"F0.wireOp",EDGE,"E26"),sQuery(id+"F0.wireOp",EDGE,"E29"),sQuery(id+"F0.wireOp",EDGE,"E30"),sQuery(id+"F0.wireOp",EDGE,"E32"),sQuery(id+"F0.wireOp",EDGE,"E33.top"),sQuery(id+"F0.wireOp",EDGE,"E34.top"),sQuery(id+"F0.wireOp",EDGE,"E40"),sQuery(id+"F0.wireOp",EDGE,"E46"),sQuery(id+"F0.wireOp",EDGE,"E35"),sQuery(id+"F0.wireOp",EDGE,"E52"),sQuery(id+"F0.wireOp",EDGE,"E1.1"),sQuery(id+"F0.wireOp",EDGE,"E1.2"),sQuery(id+"F0.wireOp",EDGE,"E1.4"),sQuery(id+"F0.wireOp",EDGE,"E1.5"),sQuery(id+"F0.wireOp",EDGE,"E56"),sQuery(id+"F0.wireOp",EDGE,"E57"),sQuery(id+"F0.wireOp",EDGE,"E58"),sQuery(id+"F0.wireOp",EDGE,"E59"),sQuery(id+"F0.wireOp",EDGE,"E60"),sQuery(id+"F0.wireOp",EDGE,"E61"),sQuery(id+"F0.wireOp",EDGE,"E62"),sQuery(id+"F0.wireOp",EDGE,"E63"),sQuery(id+"F0.wireOp",EDGE,"E64"),sQuery(id+"F0.wireOp",EDGE,"E65"),sQuery(id+"F0.wireOp",EDGE,"E66"),sQuery(id+"F0.wireOp",EDGE,"E67"),sQuery(id+"F0.wireOp",EDGE,"E68")])],"isStart":false}),makeQuery(id+"F3.opExtrude","CAP_FACE",FACE,{"disambiguationData":[OSD([sQuery(id+"F2.wireOp",EDGE,"E90"),sQuery(id+"F2.wireOp",EDGE,"E91.0"),sQuery(id+"F2.wireOp",EDGE,"E91.1"),sQuery(id+"F2.wireOp",EDGE,"E91.2"),sQuery(id+"F2.wireOp",EDGE,"E91.3"),sQuery(id+"F2.wireOp",EDGE,"E91.4"),sQuery(id+"F2.wireOp",EDGE,"E91.5")])],"isStart":false})]});
            var sketch = newSketch(context, id + "F5", { "sketchPlane" : qUnion([Q0])});
            skLineSegment(sketch, "E92.bottom", {"start": v(-20.32, 3.8) * mm, "end": v(-12.7, 3.81) * mm});
            skLineSegment(sketch, "E92.top", {"start": v(-20.32, -3.81) * mm, "end": v(-12.7, -3.81) * mm});
            skLineSegment(sketch, "E92.left", {"start": v(-20.32, 3.8) * mm, "end": v(-20.32, -3.81) * mm});
            skLineSegment(sketch, "E92.right", {"start": v(-12.7, 3.81) * mm, "end": v(-12.7, -3.8) * mm});
            skLineSegment(sketch, "E93.bottom", {"start": v(20.32, 3.81) * mm, "end": v(12.7, 3.81) * mm});
            skLineSegment(sketch, "E93.top", {"start": v(20.32, -3.8) * mm, "end": v(12.7, -3.8) * mm});
            skLineSegment(sketch, "E93.left", {"start": v(20.32, 3.81) * mm, "end": v(20.32, -3.8) * mm});
            skLineSegment(sketch, "E93.right", {"start": v(12.7, 3.81) * mm, "end": v(12.7, -3.8) * mm});
            skSolve(sketch);
        }
        {
            var Q0;
            Q0=makeQuery(id+"F5.imprint","IMPRINT",FACE,{"disambiguationData":[TD([[makeQuery(id+"F5.imprint","IMPRINT",EDGE,{"derivedFrom":sQuery(id+"F5.wireOp",EDGE,"E93.bottom")}),1.0]])]});
            var Q1;
            Q1=makeQuery(id+"F5.imprint","IMPRINT",FACE,{"disambiguationData":[TD([[makeQuery(id+"F5.imprint","IMPRINT",EDGE,{"derivedFrom":sQuery(id+"F5.wireOp",EDGE,"E92.bottom")}),-1.0]])]});
            extrude(context, id + "F6", {"entities" : qUnion([Q0, Q1]), "operationType" : NewBodyOperationType.REMOVE, "oppositeDirection" : true, "depth" : 25.4 * mm});
        }
        {
            var Q0;
            Q0=makeQuery(id+"F1.opExtrude","CAP_EDGE",EDGE,{"disambiguationData":[OSD([sQuery(id+"F0.wireOp",EDGE,"E17")])],"isStart":true});
            var Q1;
            Q1=makeQuery(id+"F1.opExtrude","CAP_EDGE",EDGE,{"disambiguationData":[OSD([sQuery(id+"F0.wireOp",EDGE,"E17")])],"isStart":false});
            var Q2;
            Q2=makeQuery(id+"F1.opExtrude","CAP_EDGE",EDGE,{"disambiguationData":[OSD([sQuery(id+"F0.wireOp",EDGE,"E15")])],"isStart":true});
            var Q3;
            Q3=makeQuery(id+"F1.opExtrude","CAP_EDGE",EDGE,{"disambiguationData":[OSD([sQuery(id+"F0.wireOp",EDGE,"E15")])],"isStart":false});
            var Q4;
            Q4=makeQuery(id+"F1.opExtrude","CAP_EDGE",EDGE,{"disambiguationData":[OSD([sQuery(id+"F0.wireOp",EDGE,"E30")])],"isStart":false});
            var Q5;
            Q5=makeQuery(id+"F1.opExtrude","CAP_EDGE",EDGE,{"disambiguationData":[OSD([sQuery(id+"F0.wireOp",EDGE,"E32")])],"isStart":false});
            var Q6;
            Q6=makeQuery(id+"F1.opExtrude","CAP_EDGE",EDGE,{"disambiguationData":[OSD([sQuery(id+"F0.wireOp",EDGE,"E30")])],"isStart":true});
            var Q7;
            Q7=makeQuery(id+"F1.opExtrude","CAP_EDGE",EDGE,{"disambiguationData":[OSD([sQuery(id+"F0.wireOp",EDGE,"E10.0"),sQuery(id+"F0.wireOp",EDGE,"E34.top")])],"isStart":false});
            var Q8;
            Q8=makeQuery(id+"F1.opExtrude","CAP_EDGE",EDGE,{"disambiguationData":[OSD([sQuery(id+"F0.wireOp",EDGE,"E10.0"),sQuery(id+"F0.wireOp",EDGE,"E34.top")])],"isStart":true});
            var Q9;
            {var subQ0=sQuery(id+"F0.wireOp",EDGE,"E10.1");Q9=makeQuery(id+"F1.opExtrude","CAP_EDGE",EDGE,{"disambiguationData":[OSD([subQ0]),TDD([makeQuery(id+"F0.imprint","IMPRINT",EDGE,{"disambiguationData":[TD([[makeQuery(id+"F0.imprint","INTERSECT",VERTEX,{"derivedFrom":[sQuery(id+"F0.wireOp",EDGE,"E10.0"),subQ0]}),-1.0]])],"derivedFrom":subQ0})])],"isStart":true});}
            var Q10;
            {var subQ0=sQuery(id+"F0.wireOp",EDGE,"E10.1");Q10=makeQuery(id+"F1.opExtrude","CAP_EDGE",EDGE,{"disambiguationData":[OSD([subQ0]),TDD([makeQuery(id+"F0.imprint","IMPRINT",EDGE,{"disambiguationData":[TD([[makeQuery(id+"F0.imprint","INTERSECT",VERTEX,{"derivedFrom":[sQuery(id+"F0.wireOp",EDGE,"E10.0"),subQ0]}),-1.0]])],"derivedFrom":subQ0})])],"isStart":false});}
            var Q11;
            {var subQ0=sQuery(id+"F0.wireOp",EDGE,"E10.5");Q11=makeQuery(id+"F1.opExtrude","CAP_EDGE",EDGE,{"disambiguationData":[OSD([subQ0]),TDD([makeQuery(id+"F0.imprint","IMPRINT",EDGE,{"disambiguationData":[TD([[makeQuery(id+"F0.imprint","INTERSECT",VERTEX,{"derivedFrom":[sQuery(id+"F0.wireOp",EDGE,"E10.0"),subQ0]}),1.0]])],"derivedFrom":subQ0})])],"isStart":true});}
            var Q12;
            {var subQ0=sQuery(id+"F0.wireOp",EDGE,"E10.5");Q12=makeQuery(id+"F1.opExtrude","CAP_EDGE",EDGE,{"disambiguationData":[OSD([subQ0]),TDD([makeQuery(id+"F0.imprint","IMPRINT",EDGE,{"disambiguationData":[TD([[makeQuery(id+"F0.imprint","INTERSECT",VERTEX,{"derivedFrom":[sQuery(id+"F0.wireOp",EDGE,"E10.0"),subQ0]}),1.0]])],"derivedFrom":subQ0})])],"isStart":false});}
            var Q13;
            {var subQ0=sQuery(id+"F0.wireOp",EDGE,"E11.1");Q13=makeQuery(id+"F1.opExtrude","CAP_EDGE",EDGE,{"disambiguationData":[OSD([subQ0]),TDD([makeQuery(id+"F0.imprint","IMPRINT",EDGE,{"disambiguationData":[TD([[makeQuery(id+"F0.imprint","INTERSECT",VERTEX,{"derivedFrom":[sQuery(id+"F0.wireOp",EDGE,"E11.0"),subQ0]}),-1.0]])],"derivedFrom":subQ0})])],"isStart":false});}
            var Q14;
            Q14=makeQuery(id+"F1.opExtrude","CAP_EDGE",EDGE,{"disambiguationData":[OSD([sQuery(id+"F0.wireOp",EDGE,"E11.0")])],"isStart":false});
            var Q15;
            Q15=makeQuery(id+"F1.opExtrude","CAP_EDGE",EDGE,{"disambiguationData":[OSD([sQuery(id+"F0.wireOp",EDGE,"E35")])],"isStart":false});
            var Q16;
            Q16=makeQuery(id+"F3.opExtrude","CAP_EDGE",EDGE,{"disambiguationData":[OSD([sQuery(id+"F2.wireOp",EDGE,"E91.1")])],"isStart":false});
            var Q17;
            Q17=makeQuery(id+"F3.opExtrude","CAP_EDGE",EDGE,{"disambiguationData":[OSD([sQuery(id+"F2.wireOp",EDGE,"E91.0")])],"isStart":false});
            var Q18;
            {var subQ0=sQuery(id+"F0.wireOp",EDGE,"E9.5");Q18=makeQuery(id+"F1.opExtrude","CAP_EDGE",EDGE,{"disambiguationData":[OSD([subQ0]),TDD([makeQuery(id+"F0.imprint","IMPRINT",EDGE,{"disambiguationData":[TD([[makeQuery(id+"F0.imprint","INTERSECT",VERTEX,{"derivedFrom":[sQuery(id+"F0.wireOp",EDGE,"E9.0"),subQ0]}),1.0]])],"derivedFrom":subQ0})])],"isStart":false});}
            var Q19;
            Q19=makeQuery(id+"F1.opExtrude","CAP_EDGE",EDGE,{"disambiguationData":[OSD([sQuery(id+"F0.wireOp",EDGE,"E9.0")])],"isStart":false});
            var Q20;
            Q20=makeQuery(id+"F1.opExtrude","CAP_EDGE",EDGE,{"disambiguationData":[OSD([sQuery(id+"F0.wireOp",EDGE,"E46")])],"isStart":false});
            var Q21;
            Q21=makeQuery(id+"F3.opExtrude","CAP_EDGE",EDGE,{"disambiguationData":[OSD([sQuery(id+"F2.wireOp",EDGE,"E91.5")])],"isStart":false});
            var Q22;
            Q22=makeQuery(id+"F6.boolean.opBoolean","COPY",EDGE,{"derivedFrom":makeQuery(id+"F6.opExtrude","CAP_EDGE",EDGE,{"disambiguationData":[OSD([sQuery(id+"F5.wireOp",EDGE,"E92.bottom")])],"isStart":true})});
            var Q23;
            Q23=makeQuery(id+"F6.boolean.opBoolean","COPY",EDGE,{"derivedFrom":makeQuery(id+"F6.opExtrude","CAP_EDGE",EDGE,{"disambiguationData":[OSD([sQuery(id+"F5.wireOp",EDGE,"E92.left")])],"isStart":true})});
            var Q24;
            Q24=makeQuery(id+"F6.boolean.opBoolean","COPY",EDGE,{"derivedFrom":makeQuery(id+"F6.opExtrude","CAP_EDGE",EDGE,{"disambiguationData":[OSD([sQuery(id+"F5.wireOp",EDGE,"E92.top")])],"isStart":true})});
            var Q25;
            Q25=makeQuery(id+"F6.boolean.opBoolean","COPY",EDGE,{"derivedFrom":makeQuery(id+"F6.opExtrude","CAP_EDGE",EDGE,{"disambiguationData":[OSD([sQuery(id+"F5.wireOp",EDGE,"E92.right")])],"isStart":true})});
            var Q26;
            Q26=makeQuery(id+"F6.boolean.opBoolean","COPY",EDGE,{"derivedFrom":makeQuery(id+"F6.opExtrude","CAP_EDGE",EDGE,{"disambiguationData":[OSD([sQuery(id+"F5.wireOp",EDGE,"E93.bottom")])],"isStart":true})});
            var Q27;
            Q27=makeQuery(id+"F6.boolean.opBoolean","COPY",EDGE,{"derivedFrom":makeQuery(id+"F6.opExtrude","CAP_EDGE",EDGE,{"disambiguationData":[OSD([sQuery(id+"F5.wireOp",EDGE,"E93.left")])],"isStart":true})});
            var Q28;
            Q28=makeQuery(id+"F6.boolean.opBoolean","COPY",EDGE,{"derivedFrom":makeQuery(id+"F6.opExtrude","CAP_EDGE",EDGE,{"disambiguationData":[OSD([sQuery(id+"F5.wireOp",EDGE,"E93.top")])],"isStart":true})});
            var Q29;
            Q29=makeQuery(id+"F1.opExtrude","CAP_EDGE",EDGE,{"disambiguationData":[OSD([sQuery(id+"F0.wireOp",EDGE,"E11.5")])],"isStart":false});
            var Q30;
            Q30=makeQuery(id+"F1.opExtrude","CAP_EDGE",EDGE,{"disambiguationData":[OSD([sQuery(id+"F0.wireOp",EDGE,"E12.1")])],"isStart":false});
            var Q31;
            Q31=makeQuery(id+"F6.boolean.opBoolean","COPY",EDGE,{"derivedFrom":makeQuery(id+"F6.opExtrude","CAP_EDGE",EDGE,{"disambiguationData":[OSD([sQuery(id+"F5.wireOp",EDGE,"E93.right")])],"isStart":true})});
            var Q32;
            Q32=makeQuery(id+"F1.opExtrude","CAP_EDGE",EDGE,{"disambiguationData":[OSD([sQuery(id+"F0.wireOp",EDGE,"E40")])],"isStart":false});
            var Q33;
            Q33=makeQuery(id+"F3.opExtrude","CAP_EDGE",EDGE,{"disambiguationData":[OSD([sQuery(id+"F2.wireOp",EDGE,"E91.2")])],"isStart":false});
            var Q34;
            Q34=makeQuery(id+"F3.opExtrude","CAP_EDGE",EDGE,{"disambiguationData":[OSD([sQuery(id+"F2.wireOp",EDGE,"E91.3")])],"isStart":false});
            var Q35;
            Q35=makeQuery(id+"F3.opExtrude","CAP_EDGE",EDGE,{"disambiguationData":[OSD([sQuery(id+"F2.wireOp",EDGE,"E91.4")])],"isStart":false});
            var Q36;
            Q36=makeQuery(id+"F1.opExtrude","CAP_EDGE",EDGE,{"disambiguationData":[OSD([sQuery(id+"F0.wireOp",EDGE,"E52")])],"isStart":false});
            var Q37;
            Q37=makeQuery(id+"F1.opExtrude","CAP_EDGE",EDGE,{"disambiguationData":[OSD([sQuery(id+"F0.wireOp",EDGE,"E14.0")])],"isStart":false});
            var Q38;
            {var subQ0=sQuery(id+"F0.wireOp",EDGE,"E14.1");Q38=makeQuery(id+"F1.opExtrude","CAP_EDGE",EDGE,{"disambiguationData":[OSD([subQ0]),TDD([makeQuery(id+"F0.imprint","IMPRINT",EDGE,{"disambiguationData":[TD([[makeQuery(id+"F0.imprint","INTERSECT",VERTEX,{"derivedFrom":[sQuery(id+"F0.wireOp",EDGE,"E14.0"),subQ0]}),-1.0]])],"derivedFrom":subQ0})])],"isStart":false});}
            var Q39;
            Q39=makeQuery(id+"F1.opExtrude","CAP_EDGE",EDGE,{"disambiguationData":[OSD([sQuery(id+"F0.wireOp",EDGE,"E23")])],"isStart":false});
            var Q40;
            {var subQ0=sQuery(id+"F0.wireOp",EDGE,"E13.5");Q40=makeQuery(id+"F1.opExtrude","CAP_EDGE",EDGE,{"disambiguationData":[OSD([subQ0]),TDD([makeQuery(id+"F0.imprint","IMPRINT",EDGE,{"disambiguationData":[TD([[makeQuery(id+"F0.imprint","INTERSECT",VERTEX,{"derivedFrom":[sQuery(id+"F0.wireOp",EDGE,"E13.0"),subQ0]}),1.0]])],"derivedFrom":subQ0})])],"isStart":false});}
            var Q41;
            Q41=makeQuery(id+"F1.opExtrude","CAP_EDGE",EDGE,{"disambiguationData":[OSD([sQuery(id+"F0.wireOp",EDGE,"E13.0"),sQuery(id+"F0.wireOp",EDGE,"E33.top")])],"isStart":false});
            var Q42;
            {var subQ0=sQuery(id+"F0.wireOp",EDGE,"E13.1");Q42=makeQuery(id+"F1.opExtrude","CAP_EDGE",EDGE,{"disambiguationData":[OSD([subQ0]),TDD([makeQuery(id+"F0.imprint","IMPRINT",EDGE,{"disambiguationData":[TD([[makeQuery(id+"F0.imprint","INTERSECT",VERTEX,{"derivedFrom":[sQuery(id+"F0.wireOp",EDGE,"E13.0"),subQ0]}),-1.0]])],"derivedFrom":subQ0})])],"isStart":false});}
            var Q43;
            Q43=makeQuery(id+"F1.opExtrude","CAP_EDGE",EDGE,{"disambiguationData":[OSD([sQuery(id+"F0.wireOp",EDGE,"E24")])],"isStart":false});
            var Q44;
            {var subQ0=sQuery(id+"F0.wireOp",EDGE,"E12.5");Q44=makeQuery(id+"F1.opExtrude","CAP_EDGE",EDGE,{"disambiguationData":[OSD([subQ0]),TDD([makeQuery(id+"F0.imprint","IMPRINT",EDGE,{"disambiguationData":[TD([[makeQuery(id+"F0.imprint","INTERSECT",VERTEX,{"derivedFrom":[sQuery(id+"F0.wireOp",EDGE,"E12.0"),subQ0]}),1.0]])],"derivedFrom":subQ0})])],"isStart":false});}
            var Q45;
            Q45=makeQuery(id+"F1.opExtrude","CAP_EDGE",EDGE,{"disambiguationData":[OSD([sQuery(id+"F0.wireOp",EDGE,"E12.0")])],"isStart":false});
            var Q46;
            Q46=makeQuery(id+"F6.boolean.opBoolean","INTERSECT",EDGE,{"derivedFrom":[makeQuery(id+"F3.boolean.opBoolean","MERGE",FACE,{"derivedFrom":[makeQuery(id+"F1.opExtrude","CAP_FACE",FACE,{"disambiguationData":[OSD([sQuery(id+"F0.wireOp",EDGE,"E3.0"),sQuery(id+"F0.wireOp",EDGE,"E3.1"),sQuery(id+"F0.wireOp",EDGE,"E3.2"),sQuery(id+"F0.wireOp",EDGE,"E3.3"),sQuery(id+"F0.wireOp",EDGE,"E3.4"),sQuery(id+"F0.wireOp",EDGE,"E3.5"),sQuery(id+"F0.wireOp",EDGE,"E4.0"),sQuery(id+"F0.wireOp",EDGE,"E4.1"),sQuery(id+"F0.wireOp",EDGE,"E4.2"),sQuery(id+"F0.wireOp",EDGE,"E4.3"),sQuery(id+"F0.wireOp",EDGE,"E4.4"),sQuery(id+"F0.wireOp",EDGE,"E4.5"),sQuery(id+"F0.wireOp",EDGE,"E5.0"),sQuery(id+"F0.wireOp",EDGE,"E5.1"),sQuery(id+"F0.wireOp",EDGE,"E5.2"),sQuery(id+"F0.wireOp",EDGE,"E5.3"),sQuery(id+"F0.wireOp",EDGE,"E5.4"),sQuery(id+"F0.wireOp",EDGE,"E5.5"),sQuery(id+"F0.wireOp",EDGE,"E6.0"),sQuery(id+"F0.wireOp",EDGE,"E6.1"),sQuery(id+"F0.wireOp",EDGE,"E6.2"),sQuery(id+"F0.wireOp",EDGE,"E6.3"),sQuery(id+"F0.wireOp",EDGE,"E6.4"),sQuery(id+"F0.wireOp",EDGE,"E6.5"),sQuery(id+"F0.wireOp",EDGE,"E7.0"),sQuery(id+"F0.wireOp",EDGE,"E7.1"),sQuery(id+"F0.wireOp",EDGE,"E7.2"),sQuery(id+"F0.wireOp",EDGE,"E7.3"),sQuery(id+"F0.wireOp",EDGE,"E7.4"),sQuery(id+"F0.wireOp",EDGE,"E7.5"),sQuery(id+"F0.wireOp",EDGE,"E8.0"),sQuery(id+"F0.wireOp",EDGE,"E8.1"),sQuery(id+"F0.wireOp",EDGE,"E8.2"),sQuery(id+"F0.wireOp",EDGE,"E8.3"),sQuery(id+"F0.wireOp",EDGE,"E8.4"),sQuery(id+"F0.wireOp",EDGE,"E8.5"),sQuery(id+"F0.wireOp",EDGE,"E9.0"),sQuery(id+"F0.wireOp",EDGE,"E9.1"),sQuery(id+"F0.wireOp",EDGE,"E9.5"),sQuery(id+"F0.wireOp",EDGE,"E10.0"),sQuery(id+"F0.wireOp",EDGE,"E10.1"),sQuery(id+"F0.wireOp",EDGE,"E10.5"),sQuery(id+"F0.wireOp",EDGE,"E11.0"),sQuery(id+"F0.wireOp",EDGE,"E11.1"),sQuery(id+"F0.wireOp",EDGE,"E11.5"),sQuery(id+"F0.wireOp",EDGE,"E12.0"),sQuery(id+"F0.wireOp",EDGE,"E12.1"),sQuery(id+"F0.wireOp",EDGE,"E12.5"),sQuery(id+"F0.wireOp",EDGE,"E13.0"),sQuery(id+"F0.wireOp",EDGE,"E13.1"),sQuery(id+"F0.wireOp",EDGE,"E13.5"),sQuery(id+"F0.wireOp",EDGE,"E14.0"),sQuery(id+"F0.wireOp",EDGE,"E14.1"),sQuery(id+"F0.wireOp",EDGE,"E14.2"),sQuery(id+"F0.wireOp",EDGE,"E14.3"),sQuery(id+"F0.wireOp",EDGE,"E14.5"),sQuery(id+"F0.wireOp",EDGE,"E15"),sQuery(id+"F0.wireOp",EDGE,"E17"),sQuery(id+"F0.wireOp",EDGE,"E18"),sQuery(id+"F0.wireOp",EDGE,"E21"),sQuery(id+"F0.wireOp",EDGE,"E23"),sQuery(id+"F0.wireOp",EDGE,"E24"),sQuery(id+"F0.wireOp",EDGE,"E26"),sQuery(id+"F0.wireOp",EDGE,"E29"),sQuery(id+"F0.wireOp",EDGE,"E30"),sQuery(id+"F0.wireOp",EDGE,"E32"),sQuery(id+"F0.wireOp",EDGE,"E33.top"),sQuery(id+"F0.wireOp",EDGE,"E34.top"),sQuery(id+"F0.wireOp",EDGE,"E40"),sQuery(id+"F0.wireOp",EDGE,"E46"),sQuery(id+"F0.wireOp",EDGE,"E35"),sQuery(id+"F0.wireOp",EDGE,"E52"),sQuery(id+"F0.wireOp",EDGE,"E1.1"),sQuery(id+"F0.wireOp",EDGE,"E1.2"),sQuery(id+"F0.wireOp",EDGE,"E1.4"),sQuery(id+"F0.wireOp",EDGE,"E1.5"),sQuery(id+"F0.wireOp",EDGE,"E56"),sQuery(id+"F0.wireOp",EDGE,"E57"),sQuery(id+"F0.wireOp",EDGE,"E58"),sQuery(id+"F0.wireOp",EDGE,"E59"),sQuery(id+"F0.wireOp",EDGE,"E60"),sQuery(id+"F0.wireOp",EDGE,"E61"),sQuery(id+"F0.wireOp",EDGE,"E62"),sQuery(id+"F0.wireOp",EDGE,"E63"),sQuery(id+"F0.wireOp",EDGE,"E64"),sQuery(id+"F0.wireOp",EDGE,"E65"),sQuery(id+"F0.wireOp",EDGE,"E66"),sQuery(id+"F0.wireOp",EDGE,"E67"),sQuery(id+"F0.wireOp",EDGE,"E68")])],"isStart":true}),makeQuery(id+"F3.opExtrude","CAP_FACE",FACE,{"disambiguationData":[OSD([sQuery(id+"F2.wireOp",EDGE,"E90"),sQuery(id+"F2.wireOp",EDGE,"E91.0"),sQuery(id+"F2.wireOp",EDGE,"E91.1"),sQuery(id+"F2.wireOp",EDGE,"E91.2"),sQuery(id+"F2.wireOp",EDGE,"E91.3"),sQuery(id+"F2.wireOp",EDGE,"E91.4"),sQuery(id+"F2.wireOp",EDGE,"E91.5")])],"isStart":true})]}),makeQuery(id+"F6.opExtrude","SWEPT_FACE",FACE,{"disambiguationData":[OSD([sQuery(id+"F5.wireOp",EDGE,"E92.right")])]})]});
            var Q47;
            Q47=makeQuery(id+"F1.opExtrude","CAP_EDGE",EDGE,{"disambiguationData":[OSD([sQuery(id+"F0.wireOp",EDGE,"E24")])],"isStart":true});
            var Q48;
            {var subQ0=sQuery(id+"F0.wireOp",EDGE,"E13.1");Q48=makeQuery(id+"F1.opExtrude","CAP_EDGE",EDGE,{"disambiguationData":[OSD([subQ0]),TDD([makeQuery(id+"F0.imprint","IMPRINT",EDGE,{"disambiguationData":[TD([[makeQuery(id+"F0.imprint","INTERSECT",VERTEX,{"derivedFrom":[sQuery(id+"F0.wireOp",EDGE,"E13.0"),subQ0]}),-1.0]])],"derivedFrom":subQ0})])],"isStart":true});}
            var Q49;
            {var subQ0=sQuery(id+"F0.wireOp",EDGE,"E13.5");Q49=makeQuery(id+"F1.opExtrude","CAP_EDGE",EDGE,{"disambiguationData":[OSD([subQ0]),TDD([makeQuery(id+"F0.imprint","IMPRINT",EDGE,{"disambiguationData":[TD([[makeQuery(id+"F0.imprint","INTERSECT",VERTEX,{"derivedFrom":[sQuery(id+"F0.wireOp",EDGE,"E13.0"),subQ0]}),1.0]])],"derivedFrom":subQ0})])],"isStart":true});}
            var Q50;
            Q50=makeQuery(id+"F1.opExtrude","CAP_EDGE",EDGE,{"disambiguationData":[OSD([sQuery(id+"F0.wireOp",EDGE,"E23")])],"isStart":true});
            var Q51;
            Q51=makeQuery(id+"F1.opExtrude","CAP_EDGE",EDGE,{"disambiguationData":[OSD([sQuery(id+"F0.wireOp",EDGE,"E21")])],"isStart":true});
            var Q52;
            Q52=makeQuery(id+"F1.opExtrude","CAP_EDGE",EDGE,{"disambiguationData":[OSD([sQuery(id+"F0.wireOp",EDGE,"E11.0")])],"isStart":true});
            var Q53;
            Q53=makeQuery(id+"F1.opExtrude","CAP_EDGE",EDGE,{"disambiguationData":[OSD([sQuery(id+"F0.wireOp",EDGE,"E35")])],"isStart":true});
            var Q54;
            {var subQ0=sQuery(id+"F0.wireOp",EDGE,"E11.1");Q54=makeQuery(id+"F1.opExtrude","CAP_EDGE",EDGE,{"disambiguationData":[OSD([subQ0]),TDD([makeQuery(id+"F0.imprint","IMPRINT",EDGE,{"disambiguationData":[TD([[makeQuery(id+"F0.imprint","INTERSECT",VERTEX,{"derivedFrom":[sQuery(id+"F0.wireOp",EDGE,"E11.0"),subQ0]}),-1.0]])],"derivedFrom":subQ0})])],"isStart":true});}
            var Q55;
            Q55=makeQuery(id+"F3.opExtrude","CAP_EDGE",EDGE,{"disambiguationData":[OSD([sQuery(id+"F2.wireOp",EDGE,"E91.5")])],"isStart":true});
            var Q56;
            Q56=makeQuery(id+"F3.opExtrude","CAP_EDGE",EDGE,{"disambiguationData":[OSD([sQuery(id+"F2.wireOp",EDGE,"E91.0")])],"isStart":true});
            var Q57;
            Q57=makeQuery(id+"F1.opExtrude","CAP_EDGE",EDGE,{"disambiguationData":[OSD([sQuery(id+"F0.wireOp",EDGE,"E46")])],"isStart":true});
            var Q58;
            Q58=makeQuery(id+"F1.opExtrude","CAP_EDGE",EDGE,{"disambiguationData":[OSD([sQuery(id+"F0.wireOp",EDGE,"E9.0")])],"isStart":true});
            var Q59;
            {var subQ0=sQuery(id+"F0.wireOp",EDGE,"E9.5");Q59=makeQuery(id+"F1.opExtrude","CAP_EDGE",EDGE,{"disambiguationData":[OSD([subQ0]),TDD([makeQuery(id+"F0.imprint","IMPRINT",EDGE,{"disambiguationData":[TD([[makeQuery(id+"F0.imprint","INTERSECT",VERTEX,{"derivedFrom":[sQuery(id+"F0.wireOp",EDGE,"E9.0"),subQ0]}),1.0]])],"derivedFrom":subQ0})])],"isStart":true});}
            var Q60;
            Q60=makeQuery(id+"F6.boolean.opBoolean","INTERSECT",EDGE,{"derivedFrom":[makeQuery(id+"F3.boolean.opBoolean","MERGE",FACE,{"derivedFrom":[makeQuery(id+"F1.opExtrude","CAP_FACE",FACE,{"disambiguationData":[OSD([sQuery(id+"F0.wireOp",EDGE,"E3.0"),sQuery(id+"F0.wireOp",EDGE,"E3.1"),sQuery(id+"F0.wireOp",EDGE,"E3.2"),sQuery(id+"F0.wireOp",EDGE,"E3.3"),sQuery(id+"F0.wireOp",EDGE,"E3.4"),sQuery(id+"F0.wireOp",EDGE,"E3.5"),sQuery(id+"F0.wireOp",EDGE,"E4.0"),sQuery(id+"F0.wireOp",EDGE,"E4.1"),sQuery(id+"F0.wireOp",EDGE,"E4.2"),sQuery(id+"F0.wireOp",EDGE,"E4.3"),sQuery(id+"F0.wireOp",EDGE,"E4.4"),sQuery(id+"F0.wireOp",EDGE,"E4.5"),sQuery(id+"F0.wireOp",EDGE,"E5.0"),sQuery(id+"F0.wireOp",EDGE,"E5.1"),sQuery(id+"F0.wireOp",EDGE,"E5.2"),sQuery(id+"F0.wireOp",EDGE,"E5.3"),sQuery(id+"F0.wireOp",EDGE,"E5.4"),sQuery(id+"F0.wireOp",EDGE,"E5.5"),sQuery(id+"F0.wireOp",EDGE,"E6.0"),sQuery(id+"F0.wireOp",EDGE,"E6.1"),sQuery(id+"F0.wireOp",EDGE,"E6.2"),sQuery(id+"F0.wireOp",EDGE,"E6.3"),sQuery(id+"F0.wireOp",EDGE,"E6.4"),sQuery(id+"F0.wireOp",EDGE,"E6.5"),sQuery(id+"F0.wireOp",EDGE,"E7.0"),sQuery(id+"F0.wireOp",EDGE,"E7.1"),sQuery(id+"F0.wireOp",EDGE,"E7.2"),sQuery(id+"F0.wireOp",EDGE,"E7.3"),sQuery(id+"F0.wireOp",EDGE,"E7.4"),sQuery(id+"F0.wireOp",EDGE,"E7.5"),sQuery(id+"F0.wireOp",EDGE,"E8.0"),sQuery(id+"F0.wireOp",EDGE,"E8.1"),sQuery(id+"F0.wireOp",EDGE,"E8.2"),sQuery(id+"F0.wireOp",EDGE,"E8.3"),sQuery(id+"F0.wireOp",EDGE,"E8.4"),sQuery(id+"F0.wireOp",EDGE,"E8.5"),sQuery(id+"F0.wireOp",EDGE,"E9.0"),sQuery(id+"F0.wireOp",EDGE,"E9.1"),sQuery(id+"F0.wireOp",EDGE,"E9.5"),sQuery(id+"F0.wireOp",EDGE,"E10.0"),sQuery(id+"F0.wireOp",EDGE,"E10.1"),sQuery(id+"F0.wireOp",EDGE,"E10.5"),sQuery(id+"F0.wireOp",EDGE,"E11.0"),sQuery(id+"F0.wireOp",EDGE,"E11.1"),sQuery(id+"F0.wireOp",EDGE,"E11.5"),sQuery(id+"F0.wireOp",EDGE,"E12.0"),sQuery(id+"F0.wireOp",EDGE,"E12.1"),sQuery(id+"F0.wireOp",EDGE,"E12.5"),sQuery(id+"F0.wireOp",EDGE,"E13.0"),sQuery(id+"F0.wireOp",EDGE,"E13.1"),sQuery(id+"F0.wireOp",EDGE,"E13.5"),sQuery(id+"F0.wireOp",EDGE,"E14.0"),sQuery(id+"F0.wireOp",EDGE,"E14.1"),sQuery(id+"F0.wireOp",EDGE,"E14.2"),sQuery(id+"F0.wireOp",EDGE,"E14.3"),sQuery(id+"F0.wireOp",EDGE,"E14.5"),sQuery(id+"F0.wireOp",EDGE,"E15"),sQuery(id+"F0.wireOp",EDGE,"E17"),sQuery(id+"F0.wireOp",EDGE,"E18"),sQuery(id+"F0.wireOp",EDGE,"E21"),sQuery(id+"F0.wireOp",EDGE,"E23"),sQuery(id+"F0.wireOp",EDGE,"E24"),sQuery(id+"F0.wireOp",EDGE,"E26"),sQuery(id+"F0.wireOp",EDGE,"E29"),sQuery(id+"F0.wireOp",EDGE,"E30"),sQuery(id+"F0.wireOp",EDGE,"E32"),sQuery(id+"F0.wireOp",EDGE,"E33.top"),sQuery(id+"F0.wireOp",EDGE,"E34.top"),sQuery(id+"F0.wireOp",EDGE,"E40"),sQuery(id+"F0.wireOp",EDGE,"E46"),sQuery(id+"F0.wireOp",EDGE,"E35"),sQuery(id+"F0.wireOp",EDGE,"E52"),sQuery(id+"F0.wireOp",EDGE,"E1.1"),sQuery(id+"F0.wireOp",EDGE,"E1.2"),sQuery(id+"F0.wireOp",EDGE,"E1.4"),sQuery(id+"F0.wireOp",EDGE,"E1.5"),sQuery(id+"F0.wireOp",EDGE,"E56"),sQuery(id+"F0.wireOp",EDGE,"E57"),sQuery(id+"F0.wireOp",EDGE,"E58"),sQuery(id+"F0.wireOp",EDGE,"E59"),sQuery(id+"F0.wireOp",EDGE,"E60"),sQuery(id+"F0.wireOp",EDGE,"E61"),sQuery(id+"F0.wireOp",EDGE,"E62"),sQuery(id+"F0.wireOp",EDGE,"E63"),sQuery(id+"F0.wireOp",EDGE,"E64"),sQuery(id+"F0.wireOp",EDGE,"E65"),sQuery(id+"F0.wireOp",EDGE,"E66"),sQuery(id+"F0.wireOp",EDGE,"E67"),sQuery(id+"F0.wireOp",EDGE,"E68")])],"isStart":true}),makeQuery(id+"F3.opExtrude","CAP_FACE",FACE,{"disambiguationData":[OSD([sQuery(id+"F2.wireOp",EDGE,"E90"),sQuery(id+"F2.wireOp",EDGE,"E91.0"),sQuery(id+"F2.wireOp",EDGE,"E91.1"),sQuery(id+"F2.wireOp",EDGE,"E91.2"),sQuery(id+"F2.wireOp",EDGE,"E91.3"),sQuery(id+"F2.wireOp",EDGE,"E91.4"),sQuery(id+"F2.wireOp",EDGE,"E91.5")])],"isStart":true})]}),makeQuery(id+"F6.opExtrude","SWEPT_FACE",FACE,{"disambiguationData":[OSD([sQuery(id+"F5.wireOp",EDGE,"E93.top")])]})]});
            var Q61;
            Q61=makeQuery(id+"F6.boolean.opBoolean","INTERSECT",EDGE,{"derivedFrom":[makeQuery(id+"F3.boolean.opBoolean","MERGE",FACE,{"derivedFrom":[makeQuery(id+"F1.opExtrude","CAP_FACE",FACE,{"disambiguationData":[OSD([sQuery(id+"F0.wireOp",EDGE,"E3.0"),sQuery(id+"F0.wireOp",EDGE,"E3.1"),sQuery(id+"F0.wireOp",EDGE,"E3.2"),sQuery(id+"F0.wireOp",EDGE,"E3.3"),sQuery(id+"F0.wireOp",EDGE,"E3.4"),sQuery(id+"F0.wireOp",EDGE,"E3.5"),sQuery(id+"F0.wireOp",EDGE,"E4.0"),sQuery(id+"F0.wireOp",EDGE,"E4.1"),sQuery(id+"F0.wireOp",EDGE,"E4.2"),sQuery(id+"F0.wireOp",EDGE,"E4.3"),sQuery(id+"F0.wireOp",EDGE,"E4.4"),sQuery(id+"F0.wireOp",EDGE,"E4.5"),sQuery(id+"F0.wireOp",EDGE,"E5.0"),sQuery(id+"F0.wireOp",EDGE,"E5.1"),sQuery(id+"F0.wireOp",EDGE,"E5.2"),sQuery(id+"F0.wireOp",EDGE,"E5.3"),sQuery(id+"F0.wireOp",EDGE,"E5.4"),sQuery(id+"F0.wireOp",EDGE,"E5.5"),sQuery(id+"F0.wireOp",EDGE,"E6.0"),sQuery(id+"F0.wireOp",EDGE,"E6.1"),sQuery(id+"F0.wireOp",EDGE,"E6.2"),sQuery(id+"F0.wireOp",EDGE,"E6.3"),sQuery(id+"F0.wireOp",EDGE,"E6.4"),sQuery(id+"F0.wireOp",EDGE,"E6.5"),sQuery(id+"F0.wireOp",EDGE,"E7.0"),sQuery(id+"F0.wireOp",EDGE,"E7.1"),sQuery(id+"F0.wireOp",EDGE,"E7.2"),sQuery(id+"F0.wireOp",EDGE,"E7.3"),sQuery(id+"F0.wireOp",EDGE,"E7.4"),sQuery(id+"F0.wireOp",EDGE,"E7.5"),sQuery(id+"F0.wireOp",EDGE,"E8.0"),sQuery(id+"F0.wireOp",EDGE,"E8.1"),sQuery(id+"F0.wireOp",EDGE,"E8.2"),sQuery(id+"F0.wireOp",EDGE,"E8.3"),sQuery(id+"F0.wireOp",EDGE,"E8.4"),sQuery(id+"F0.wireOp",EDGE,"E8.5"),sQuery(id+"F0.wireOp",EDGE,"E9.0"),sQuery(id+"F0.wireOp",EDGE,"E9.1"),sQuery(id+"F0.wireOp",EDGE,"E9.5"),sQuery(id+"F0.wireOp",EDGE,"E10.0"),sQuery(id+"F0.wireOp",EDGE,"E10.1"),sQuery(id+"F0.wireOp",EDGE,"E10.5"),sQuery(id+"F0.wireOp",EDGE,"E11.0"),sQuery(id+"F0.wireOp",EDGE,"E11.1"),sQuery(id+"F0.wireOp",EDGE,"E11.5"),sQuery(id+"F0.wireOp",EDGE,"E12.0"),sQuery(id+"F0.wireOp",EDGE,"E12.1"),sQuery(id+"F0.wireOp",EDGE,"E12.5"),sQuery(id+"F0.wireOp",EDGE,"E13.0"),sQuery(id+"F0.wireOp",EDGE,"E13.1"),sQuery(id+"F0.wireOp",EDGE,"E13.5"),sQuery(id+"F0.wireOp",EDGE,"E14.0"),sQuery(id+"F0.wireOp",EDGE,"E14.1"),sQuery(id+"F0.wireOp",EDGE,"E14.2"),sQuery(id+"F0.wireOp",EDGE,"E14.3"),sQuery(id+"F0.wireOp",EDGE,"E14.5"),sQuery(id+"F0.wireOp",EDGE,"E15"),sQuery(id+"F0.wireOp",EDGE,"E17"),sQuery(id+"F0.wireOp",EDGE,"E18"),sQuery(id+"F0.wireOp",EDGE,"E21"),sQuery(id+"F0.wireOp",EDGE,"E23"),sQuery(id+"F0.wireOp",EDGE,"E24"),sQuery(id+"F0.wireOp",EDGE,"E26"),sQuery(id+"F0.wireOp",EDGE,"E29"),sQuery(id+"F0.wireOp",EDGE,"E30"),sQuery(id+"F0.wireOp",EDGE,"E32"),sQuery(id+"F0.wireOp",EDGE,"E33.top"),sQuery(id+"F0.wireOp",EDGE,"E34.top"),sQuery(id+"F0.wireOp",EDGE,"E40"),sQuery(id+"F0.wireOp",EDGE,"E46"),sQuery(id+"F0.wireOp",EDGE,"E35"),sQuery(id+"F0.wireOp",EDGE,"E52"),sQuery(id+"F0.wireOp",EDGE,"E1.1"),sQuery(id+"F0.wireOp",EDGE,"E1.2"),sQuery(id+"F0.wireOp",EDGE,"E1.4"),sQuery(id+"F0.wireOp",EDGE,"E1.5"),sQuery(id+"F0.wireOp",EDGE,"E56"),sQuery(id+"F0.wireOp",EDGE,"E57"),sQuery(id+"F0.wireOp",EDGE,"E58"),sQuery(id+"F0.wireOp",EDGE,"E59"),sQuery(id+"F0.wireOp",EDGE,"E60"),sQuery(id+"F0.wireOp",EDGE,"E61"),sQuery(id+"F0.wireOp",EDGE,"E62"),sQuery(id+"F0.wireOp",EDGE,"E63"),sQuery(id+"F0.wireOp",EDGE,"E64"),sQuery(id+"F0.wireOp",EDGE,"E65"),sQuery(id+"F0.wireOp",EDGE,"E66"),sQuery(id+"F0.wireOp",EDGE,"E67"),sQuery(id+"F0.wireOp",EDGE,"E68")])],"isStart":true}),makeQuery(id+"F3.opExtrude","CAP_FACE",FACE,{"disambiguationData":[OSD([sQuery(id+"F2.wireOp",EDGE,"E90"),sQuery(id+"F2.wireOp",EDGE,"E91.0"),sQuery(id+"F2.wireOp",EDGE,"E91.1"),sQuery(id+"F2.wireOp",EDGE,"E91.2"),sQuery(id+"F2.wireOp",EDGE,"E91.3"),sQuery(id+"F2.wireOp",EDGE,"E91.4"),sQuery(id+"F2.wireOp",EDGE,"E91.5")])],"isStart":true})]}),makeQuery(id+"F6.opExtrude","SWEPT_FACE",FACE,{"disambiguationData":[OSD([sQuery(id+"F5.wireOp",EDGE,"E93.bottom")])]})]});
            var Q62;
            Q62=makeQuery(id+"F6.boolean.opBoolean","INTERSECT",EDGE,{"derivedFrom":[makeQuery(id+"F3.boolean.opBoolean","MERGE",FACE,{"derivedFrom":[makeQuery(id+"F1.opExtrude","CAP_FACE",FACE,{"disambiguationData":[OSD([sQuery(id+"F0.wireOp",EDGE,"E3.0"),sQuery(id+"F0.wireOp",EDGE,"E3.1"),sQuery(id+"F0.wireOp",EDGE,"E3.2"),sQuery(id+"F0.wireOp",EDGE,"E3.3"),sQuery(id+"F0.wireOp",EDGE,"E3.4"),sQuery(id+"F0.wireOp",EDGE,"E3.5"),sQuery(id+"F0.wireOp",EDGE,"E4.0"),sQuery(id+"F0.wireOp",EDGE,"E4.1"),sQuery(id+"F0.wireOp",EDGE,"E4.2"),sQuery(id+"F0.wireOp",EDGE,"E4.3"),sQuery(id+"F0.wireOp",EDGE,"E4.4"),sQuery(id+"F0.wireOp",EDGE,"E4.5"),sQuery(id+"F0.wireOp",EDGE,"E5.0"),sQuery(id+"F0.wireOp",EDGE,"E5.1"),sQuery(id+"F0.wireOp",EDGE,"E5.2"),sQuery(id+"F0.wireOp",EDGE,"E5.3"),sQuery(id+"F0.wireOp",EDGE,"E5.4"),sQuery(id+"F0.wireOp",EDGE,"E5.5"),sQuery(id+"F0.wireOp",EDGE,"E6.0"),sQuery(id+"F0.wireOp",EDGE,"E6.1"),sQuery(id+"F0.wireOp",EDGE,"E6.2"),sQuery(id+"F0.wireOp",EDGE,"E6.3"),sQuery(id+"F0.wireOp",EDGE,"E6.4"),sQuery(id+"F0.wireOp",EDGE,"E6.5"),sQuery(id+"F0.wireOp",EDGE,"E7.0"),sQuery(id+"F0.wireOp",EDGE,"E7.1"),sQuery(id+"F0.wireOp",EDGE,"E7.2"),sQuery(id+"F0.wireOp",EDGE,"E7.3"),sQuery(id+"F0.wireOp",EDGE,"E7.4"),sQuery(id+"F0.wireOp",EDGE,"E7.5"),sQuery(id+"F0.wireOp",EDGE,"E8.0"),sQuery(id+"F0.wireOp",EDGE,"E8.1"),sQuery(id+"F0.wireOp",EDGE,"E8.2"),sQuery(id+"F0.wireOp",EDGE,"E8.3"),sQuery(id+"F0.wireOp",EDGE,"E8.4"),sQuery(id+"F0.wireOp",EDGE,"E8.5"),sQuery(id+"F0.wireOp",EDGE,"E9.0"),sQuery(id+"F0.wireOp",EDGE,"E9.1"),sQuery(id+"F0.wireOp",EDGE,"E9.5"),sQuery(id+"F0.wireOp",EDGE,"E10.0"),sQuery(id+"F0.wireOp",EDGE,"E10.1"),sQuery(id+"F0.wireOp",EDGE,"E10.5"),sQuery(id+"F0.wireOp",EDGE,"E11.0"),sQuery(id+"F0.wireOp",EDGE,"E11.1"),sQuery(id+"F0.wireOp",EDGE,"E11.5"),sQuery(id+"F0.wireOp",EDGE,"E12.0"),sQuery(id+"F0.wireOp",EDGE,"E12.1"),sQuery(id+"F0.wireOp",EDGE,"E12.5"),sQuery(id+"F0.wireOp",EDGE,"E13.0"),sQuery(id+"F0.wireOp",EDGE,"E13.1"),sQuery(id+"F0.wireOp",EDGE,"E13.5"),sQuery(id+"F0.wireOp",EDGE,"E14.0"),sQuery(id+"F0.wireOp",EDGE,"E14.1"),sQuery(id+"F0.wireOp",EDGE,"E14.2"),sQuery(id+"F0.wireOp",EDGE,"E14.3"),sQuery(id+"F0.wireOp",EDGE,"E14.5"),sQuery(id+"F0.wireOp",EDGE,"E15"),sQuery(id+"F0.wireOp",EDGE,"E17"),sQuery(id+"F0.wireOp",EDGE,"E18"),sQuery(id+"F0.wireOp",EDGE,"E21"),sQuery(id+"F0.wireOp",EDGE,"E23"),sQuery(id+"F0.wireOp",EDGE,"E24"),sQuery(id+"F0.wireOp",EDGE,"E26"),sQuery(id+"F0.wireOp",EDGE,"E29"),sQuery(id+"F0.wireOp",EDGE,"E30"),sQuery(id+"F0.wireOp",EDGE,"E32"),sQuery(id+"F0.wireOp",EDGE,"E33.top"),sQuery(id+"F0.wireOp",EDGE,"E34.top"),sQuery(id+"F0.wireOp",EDGE,"E40"),sQuery(id+"F0.wireOp",EDGE,"E46"),sQuery(id+"F0.wireOp",EDGE,"E35"),sQuery(id+"F0.wireOp",EDGE,"E52"),sQuery(id+"F0.wireOp",EDGE,"E1.1"),sQuery(id+"F0.wireOp",EDGE,"E1.2"),sQuery(id+"F0.wireOp",EDGE,"E1.4"),sQuery(id+"F0.wireOp",EDGE,"E1.5"),sQuery(id+"F0.wireOp",EDGE,"E56"),sQuery(id+"F0.wireOp",EDGE,"E57"),sQuery(id+"F0.wireOp",EDGE,"E58"),sQuery(id+"F0.wireOp",EDGE,"E59"),sQuery(id+"F0.wireOp",EDGE,"E60"),sQuery(id+"F0.wireOp",EDGE,"E61"),sQuery(id+"F0.wireOp",EDGE,"E62"),sQuery(id+"F0.wireOp",EDGE,"E63"),sQuery(id+"F0.wireOp",EDGE,"E64"),sQuery(id+"F0.wireOp",EDGE,"E65"),sQuery(id+"F0.wireOp",EDGE,"E66"),sQuery(id+"F0.wireOp",EDGE,"E67"),sQuery(id+"F0.wireOp",EDGE,"E68")])],"isStart":true}),makeQuery(id+"F3.opExtrude","CAP_FACE",FACE,{"disambiguationData":[OSD([sQuery(id+"F2.wireOp",EDGE,"E90"),sQuery(id+"F2.wireOp",EDGE,"E91.0"),sQuery(id+"F2.wireOp",EDGE,"E91.1"),sQuery(id+"F2.wireOp",EDGE,"E91.2"),sQuery(id+"F2.wireOp",EDGE,"E91.3"),sQuery(id+"F2.wireOp",EDGE,"E91.4"),sQuery(id+"F2.wireOp",EDGE,"E91.5")])],"isStart":true})]}),makeQuery(id+"F6.opExtrude","SWEPT_FACE",FACE,{"disambiguationData":[OSD([sQuery(id+"F5.wireOp",EDGE,"E93.right")])]})]});
            var Q63;
            Q63=makeQuery(id+"F6.boolean.opBoolean","INTERSECT",EDGE,{"derivedFrom":[makeQuery(id+"F3.boolean.opBoolean","MERGE",FACE,{"derivedFrom":[makeQuery(id+"F1.opExtrude","CAP_FACE",FACE,{"disambiguationData":[OSD([sQuery(id+"F0.wireOp",EDGE,"E3.0"),sQuery(id+"F0.wireOp",EDGE,"E3.1"),sQuery(id+"F0.wireOp",EDGE,"E3.2"),sQuery(id+"F0.wireOp",EDGE,"E3.3"),sQuery(id+"F0.wireOp",EDGE,"E3.4"),sQuery(id+"F0.wireOp",EDGE,"E3.5"),sQuery(id+"F0.wireOp",EDGE,"E4.0"),sQuery(id+"F0.wireOp",EDGE,"E4.1"),sQuery(id+"F0.wireOp",EDGE,"E4.2"),sQuery(id+"F0.wireOp",EDGE,"E4.3"),sQuery(id+"F0.wireOp",EDGE,"E4.4"),sQuery(id+"F0.wireOp",EDGE,"E4.5"),sQuery(id+"F0.wireOp",EDGE,"E5.0"),sQuery(id+"F0.wireOp",EDGE,"E5.1"),sQuery(id+"F0.wireOp",EDGE,"E5.2"),sQuery(id+"F0.wireOp",EDGE,"E5.3"),sQuery(id+"F0.wireOp",EDGE,"E5.4"),sQuery(id+"F0.wireOp",EDGE,"E5.5"),sQuery(id+"F0.wireOp",EDGE,"E6.0"),sQuery(id+"F0.wireOp",EDGE,"E6.1"),sQuery(id+"F0.wireOp",EDGE,"E6.2"),sQuery(id+"F0.wireOp",EDGE,"E6.3"),sQuery(id+"F0.wireOp",EDGE,"E6.4"),sQuery(id+"F0.wireOp",EDGE,"E6.5"),sQuery(id+"F0.wireOp",EDGE,"E7.0"),sQuery(id+"F0.wireOp",EDGE,"E7.1"),sQuery(id+"F0.wireOp",EDGE,"E7.2"),sQuery(id+"F0.wireOp",EDGE,"E7.3"),sQuery(id+"F0.wireOp",EDGE,"E7.4"),sQuery(id+"F0.wireOp",EDGE,"E7.5"),sQuery(id+"F0.wireOp",EDGE,"E8.0"),sQuery(id+"F0.wireOp",EDGE,"E8.1"),sQuery(id+"F0.wireOp",EDGE,"E8.2"),sQuery(id+"F0.wireOp",EDGE,"E8.3"),sQuery(id+"F0.wireOp",EDGE,"E8.4"),sQuery(id+"F0.wireOp",EDGE,"E8.5"),sQuery(id+"F0.wireOp",EDGE,"E9.0"),sQuery(id+"F0.wireOp",EDGE,"E9.1"),sQuery(id+"F0.wireOp",EDGE,"E9.5"),sQuery(id+"F0.wireOp",EDGE,"E10.0"),sQuery(id+"F0.wireOp",EDGE,"E10.1"),sQuery(id+"F0.wireOp",EDGE,"E10.5"),sQuery(id+"F0.wireOp",EDGE,"E11.0"),sQuery(id+"F0.wireOp",EDGE,"E11.1"),sQuery(id+"F0.wireOp",EDGE,"E11.5"),sQuery(id+"F0.wireOp",EDGE,"E12.0"),sQuery(id+"F0.wireOp",EDGE,"E12.1"),sQuery(id+"F0.wireOp",EDGE,"E12.5"),sQuery(id+"F0.wireOp",EDGE,"E13.0"),sQuery(id+"F0.wireOp",EDGE,"E13.1"),sQuery(id+"F0.wireOp",EDGE,"E13.5"),sQuery(id+"F0.wireOp",EDGE,"E14.0"),sQuery(id+"F0.wireOp",EDGE,"E14.1"),sQuery(id+"F0.wireOp",EDGE,"E14.2"),sQuery(id+"F0.wireOp",EDGE,"E14.3"),sQuery(id+"F0.wireOp",EDGE,"E14.5"),sQuery(id+"F0.wireOp",EDGE,"E15"),sQuery(id+"F0.wireOp",EDGE,"E17"),sQuery(id+"F0.wireOp",EDGE,"E18"),sQuery(id+"F0.wireOp",EDGE,"E21"),sQuery(id+"F0.wireOp",EDGE,"E23"),sQuery(id+"F0.wireOp",EDGE,"E24"),sQuery(id+"F0.wireOp",EDGE,"E26"),sQuery(id+"F0.wireOp",EDGE,"E29"),sQuery(id+"F0.wireOp",EDGE,"E30"),sQuery(id+"F0.wireOp",EDGE,"E32"),sQuery(id+"F0.wireOp",EDGE,"E33.top"),sQuery(id+"F0.wireOp",EDGE,"E34.top"),sQuery(id+"F0.wireOp",EDGE,"E40"),sQuery(id+"F0.wireOp",EDGE,"E46"),sQuery(id+"F0.wireOp",EDGE,"E35"),sQuery(id+"F0.wireOp",EDGE,"E52"),sQuery(id+"F0.wireOp",EDGE,"E1.1"),sQuery(id+"F0.wireOp",EDGE,"E1.2"),sQuery(id+"F0.wireOp",EDGE,"E1.4"),sQuery(id+"F0.wireOp",EDGE,"E1.5"),sQuery(id+"F0.wireOp",EDGE,"E56"),sQuery(id+"F0.wireOp",EDGE,"E57"),sQuery(id+"F0.wireOp",EDGE,"E58"),sQuery(id+"F0.wireOp",EDGE,"E59"),sQuery(id+"F0.wireOp",EDGE,"E60"),sQuery(id+"F0.wireOp",EDGE,"E61"),sQuery(id+"F0.wireOp",EDGE,"E62"),sQuery(id+"F0.wireOp",EDGE,"E63"),sQuery(id+"F0.wireOp",EDGE,"E64"),sQuery(id+"F0.wireOp",EDGE,"E65"),sQuery(id+"F0.wireOp",EDGE,"E66"),sQuery(id+"F0.wireOp",EDGE,"E67"),sQuery(id+"F0.wireOp",EDGE,"E68")])],"isStart":true}),makeQuery(id+"F3.opExtrude","CAP_FACE",FACE,{"disambiguationData":[OSD([sQuery(id+"F2.wireOp",EDGE,"E90"),sQuery(id+"F2.wireOp",EDGE,"E91.0"),sQuery(id+"F2.wireOp",EDGE,"E91.1"),sQuery(id+"F2.wireOp",EDGE,"E91.2"),sQuery(id+"F2.wireOp",EDGE,"E91.3"),sQuery(id+"F2.wireOp",EDGE,"E91.4"),sQuery(id+"F2.wireOp",EDGE,"E91.5")])],"isStart":true})]}),makeQuery(id+"F6.opExtrude","SWEPT_FACE",FACE,{"disambiguationData":[OSD([sQuery(id+"F5.wireOp",EDGE,"E93.left")])]})]});
            var Q64;
            Q64=makeQuery(id+"F6.boolean.opBoolean","INTERSECT",EDGE,{"derivedFrom":[makeQuery(id+"F3.boolean.opBoolean","MERGE",FACE,{"derivedFrom":[makeQuery(id+"F1.opExtrude","CAP_FACE",FACE,{"disambiguationData":[OSD([sQuery(id+"F0.wireOp",EDGE,"E3.0"),sQuery(id+"F0.wireOp",EDGE,"E3.1"),sQuery(id+"F0.wireOp",EDGE,"E3.2"),sQuery(id+"F0.wireOp",EDGE,"E3.3"),sQuery(id+"F0.wireOp",EDGE,"E3.4"),sQuery(id+"F0.wireOp",EDGE,"E3.5"),sQuery(id+"F0.wireOp",EDGE,"E4.0"),sQuery(id+"F0.wireOp",EDGE,"E4.1"),sQuery(id+"F0.wireOp",EDGE,"E4.2"),sQuery(id+"F0.wireOp",EDGE,"E4.3"),sQuery(id+"F0.wireOp",EDGE,"E4.4"),sQuery(id+"F0.wireOp",EDGE,"E4.5"),sQuery(id+"F0.wireOp",EDGE,"E5.0"),sQuery(id+"F0.wireOp",EDGE,"E5.1"),sQuery(id+"F0.wireOp",EDGE,"E5.2"),sQuery(id+"F0.wireOp",EDGE,"E5.3"),sQuery(id+"F0.wireOp",EDGE,"E5.4"),sQuery(id+"F0.wireOp",EDGE,"E5.5"),sQuery(id+"F0.wireOp",EDGE,"E6.0"),sQuery(id+"F0.wireOp",EDGE,"E6.1"),sQuery(id+"F0.wireOp",EDGE,"E6.2"),sQuery(id+"F0.wireOp",EDGE,"E6.3"),sQuery(id+"F0.wireOp",EDGE,"E6.4"),sQuery(id+"F0.wireOp",EDGE,"E6.5"),sQuery(id+"F0.wireOp",EDGE,"E7.0"),sQuery(id+"F0.wireOp",EDGE,"E7.1"),sQuery(id+"F0.wireOp",EDGE,"E7.2"),sQuery(id+"F0.wireOp",EDGE,"E7.3"),sQuery(id+"F0.wireOp",EDGE,"E7.4"),sQuery(id+"F0.wireOp",EDGE,"E7.5"),sQuery(id+"F0.wireOp",EDGE,"E8.0"),sQuery(id+"F0.wireOp",EDGE,"E8.1"),sQuery(id+"F0.wireOp",EDGE,"E8.2"),sQuery(id+"F0.wireOp",EDGE,"E8.3"),sQuery(id+"F0.wireOp",EDGE,"E8.4"),sQuery(id+"F0.wireOp",EDGE,"E8.5"),sQuery(id+"F0.wireOp",EDGE,"E9.0"),sQuery(id+"F0.wireOp",EDGE,"E9.1"),sQuery(id+"F0.wireOp",EDGE,"E9.5"),sQuery(id+"F0.wireOp",EDGE,"E10.0"),sQuery(id+"F0.wireOp",EDGE,"E10.1"),sQuery(id+"F0.wireOp",EDGE,"E10.5"),sQuery(id+"F0.wireOp",EDGE,"E11.0"),sQuery(id+"F0.wireOp",EDGE,"E11.1"),sQuery(id+"F0.wireOp",EDGE,"E11.5"),sQuery(id+"F0.wireOp",EDGE,"E12.0"),sQuery(id+"F0.wireOp",EDGE,"E12.1"),sQuery(id+"F0.wireOp",EDGE,"E12.5"),sQuery(id+"F0.wireOp",EDGE,"E13.0"),sQuery(id+"F0.wireOp",EDGE,"E13.1"),sQuery(id+"F0.wireOp",EDGE,"E13.5"),sQuery(id+"F0.wireOp",EDGE,"E14.0"),sQuery(id+"F0.wireOp",EDGE,"E14.1"),sQuery(id+"F0.wireOp",EDGE,"E14.2"),sQuery(id+"F0.wireOp",EDGE,"E14.3"),sQuery(id+"F0.wireOp",EDGE,"E14.5"),sQuery(id+"F0.wireOp",EDGE,"E15"),sQuery(id+"F0.wireOp",EDGE,"E17"),sQuery(id+"F0.wireOp",EDGE,"E18"),sQuery(id+"F0.wireOp",EDGE,"E21"),sQuery(id+"F0.wireOp",EDGE,"E23"),sQuery(id+"F0.wireOp",EDGE,"E24"),sQuery(id+"F0.wireOp",EDGE,"E26"),sQuery(id+"F0.wireOp",EDGE,"E29"),sQuery(id+"F0.wireOp",EDGE,"E30"),sQuery(id+"F0.wireOp",EDGE,"E32"),sQuery(id+"F0.wireOp",EDGE,"E33.top"),sQuery(id+"F0.wireOp",EDGE,"E34.top"),sQuery(id+"F0.wireOp",EDGE,"E40"),sQuery(id+"F0.wireOp",EDGE,"E46"),sQuery(id+"F0.wireOp",EDGE,"E35"),sQuery(id+"F0.wireOp",EDGE,"E52"),sQuery(id+"F0.wireOp",EDGE,"E1.1"),sQuery(id+"F0.wireOp",EDGE,"E1.2"),sQuery(id+"F0.wireOp",EDGE,"E1.4"),sQuery(id+"F0.wireOp",EDGE,"E1.5"),sQuery(id+"F0.wireOp",EDGE,"E56"),sQuery(id+"F0.wireOp",EDGE,"E57"),sQuery(id+"F0.wireOp",EDGE,"E58"),sQuery(id+"F0.wireOp",EDGE,"E59"),sQuery(id+"F0.wireOp",EDGE,"E60"),sQuery(id+"F0.wireOp",EDGE,"E61"),sQuery(id+"F0.wireOp",EDGE,"E62"),sQuery(id+"F0.wireOp",EDGE,"E63"),sQuery(id+"F0.wireOp",EDGE,"E64"),sQuery(id+"F0.wireOp",EDGE,"E65"),sQuery(id+"F0.wireOp",EDGE,"E66"),sQuery(id+"F0.wireOp",EDGE,"E67"),sQuery(id+"F0.wireOp",EDGE,"E68")])],"isStart":true}),makeQuery(id+"F3.opExtrude","CAP_FACE",FACE,{"disambiguationData":[OSD([sQuery(id+"F2.wireOp",EDGE,"E90"),sQuery(id+"F2.wireOp",EDGE,"E91.0"),sQuery(id+"F2.wireOp",EDGE,"E91.1"),sQuery(id+"F2.wireOp",EDGE,"E91.2"),sQuery(id+"F2.wireOp",EDGE,"E91.3"),sQuery(id+"F2.wireOp",EDGE,"E91.4"),sQuery(id+"F2.wireOp",EDGE,"E91.5")])],"isStart":true})]}),makeQuery(id+"F6.opExtrude","SWEPT_FACE",FACE,{"disambiguationData":[OSD([sQuery(id+"F5.wireOp",EDGE,"E92.bottom")])]})]});
            var Q65;
            Q65=makeQuery(id+"F6.boolean.opBoolean","INTERSECT",EDGE,{"derivedFrom":[makeQuery(id+"F3.boolean.opBoolean","MERGE",FACE,{"derivedFrom":[makeQuery(id+"F1.opExtrude","CAP_FACE",FACE,{"disambiguationData":[OSD([sQuery(id+"F0.wireOp",EDGE,"E3.0"),sQuery(id+"F0.wireOp",EDGE,"E3.1"),sQuery(id+"F0.wireOp",EDGE,"E3.2"),sQuery(id+"F0.wireOp",EDGE,"E3.3"),sQuery(id+"F0.wireOp",EDGE,"E3.4"),sQuery(id+"F0.wireOp",EDGE,"E3.5"),sQuery(id+"F0.wireOp",EDGE,"E4.0"),sQuery(id+"F0.wireOp",EDGE,"E4.1"),sQuery(id+"F0.wireOp",EDGE,"E4.2"),sQuery(id+"F0.wireOp",EDGE,"E4.3"),sQuery(id+"F0.wireOp",EDGE,"E4.4"),sQuery(id+"F0.wireOp",EDGE,"E4.5"),sQuery(id+"F0.wireOp",EDGE,"E5.0"),sQuery(id+"F0.wireOp",EDGE,"E5.1"),sQuery(id+"F0.wireOp",EDGE,"E5.2"),sQuery(id+"F0.wireOp",EDGE,"E5.3"),sQuery(id+"F0.wireOp",EDGE,"E5.4"),sQuery(id+"F0.wireOp",EDGE,"E5.5"),sQuery(id+"F0.wireOp",EDGE,"E6.0"),sQuery(id+"F0.wireOp",EDGE,"E6.1"),sQuery(id+"F0.wireOp",EDGE,"E6.2"),sQuery(id+"F0.wireOp",EDGE,"E6.3"),sQuery(id+"F0.wireOp",EDGE,"E6.4"),sQuery(id+"F0.wireOp",EDGE,"E6.5"),sQuery(id+"F0.wireOp",EDGE,"E7.0"),sQuery(id+"F0.wireOp",EDGE,"E7.1"),sQuery(id+"F0.wireOp",EDGE,"E7.2"),sQuery(id+"F0.wireOp",EDGE,"E7.3"),sQuery(id+"F0.wireOp",EDGE,"E7.4"),sQuery(id+"F0.wireOp",EDGE,"E7.5"),sQuery(id+"F0.wireOp",EDGE,"E8.0"),sQuery(id+"F0.wireOp",EDGE,"E8.1"),sQuery(id+"F0.wireOp",EDGE,"E8.2"),sQuery(id+"F0.wireOp",EDGE,"E8.3"),sQuery(id+"F0.wireOp",EDGE,"E8.4"),sQuery(id+"F0.wireOp",EDGE,"E8.5"),sQuery(id+"F0.wireOp",EDGE,"E9.0"),sQuery(id+"F0.wireOp",EDGE,"E9.1"),sQuery(id+"F0.wireOp",EDGE,"E9.5"),sQuery(id+"F0.wireOp",EDGE,"E10.0"),sQuery(id+"F0.wireOp",EDGE,"E10.1"),sQuery(id+"F0.wireOp",EDGE,"E10.5"),sQuery(id+"F0.wireOp",EDGE,"E11.0"),sQuery(id+"F0.wireOp",EDGE,"E11.1"),sQuery(id+"F0.wireOp",EDGE,"E11.5"),sQuery(id+"F0.wireOp",EDGE,"E12.0"),sQuery(id+"F0.wireOp",EDGE,"E12.1"),sQuery(id+"F0.wireOp",EDGE,"E12.5"),sQuery(id+"F0.wireOp",EDGE,"E13.0"),sQuery(id+"F0.wireOp",EDGE,"E13.1"),sQuery(id+"F0.wireOp",EDGE,"E13.5"),sQuery(id+"F0.wireOp",EDGE,"E14.0"),sQuery(id+"F0.wireOp",EDGE,"E14.1"),sQuery(id+"F0.wireOp",EDGE,"E14.2"),sQuery(id+"F0.wireOp",EDGE,"E14.3"),sQuery(id+"F0.wireOp",EDGE,"E14.5"),sQuery(id+"F0.wireOp",EDGE,"E15"),sQuery(id+"F0.wireOp",EDGE,"E17"),sQuery(id+"F0.wireOp",EDGE,"E18"),sQuery(id+"F0.wireOp",EDGE,"E21"),sQuery(id+"F0.wireOp",EDGE,"E23"),sQuery(id+"F0.wireOp",EDGE,"E24"),sQuery(id+"F0.wireOp",EDGE,"E26"),sQuery(id+"F0.wireOp",EDGE,"E29"),sQuery(id+"F0.wireOp",EDGE,"E30"),sQuery(id+"F0.wireOp",EDGE,"E32"),sQuery(id+"F0.wireOp",EDGE,"E33.top"),sQuery(id+"F0.wireOp",EDGE,"E34.top"),sQuery(id+"F0.wireOp",EDGE,"E40"),sQuery(id+"F0.wireOp",EDGE,"E46"),sQuery(id+"F0.wireOp",EDGE,"E35"),sQuery(id+"F0.wireOp",EDGE,"E52"),sQuery(id+"F0.wireOp",EDGE,"E1.1"),sQuery(id+"F0.wireOp",EDGE,"E1.2"),sQuery(id+"F0.wireOp",EDGE,"E1.4"),sQuery(id+"F0.wireOp",EDGE,"E1.5"),sQuery(id+"F0.wireOp",EDGE,"E56"),sQuery(id+"F0.wireOp",EDGE,"E57"),sQuery(id+"F0.wireOp",EDGE,"E58"),sQuery(id+"F0.wireOp",EDGE,"E59"),sQuery(id+"F0.wireOp",EDGE,"E60"),sQuery(id+"F0.wireOp",EDGE,"E61"),sQuery(id+"F0.wireOp",EDGE,"E62"),sQuery(id+"F0.wireOp",EDGE,"E63"),sQuery(id+"F0.wireOp",EDGE,"E64"),sQuery(id+"F0.wireOp",EDGE,"E65"),sQuery(id+"F0.wireOp",EDGE,"E66"),sQuery(id+"F0.wireOp",EDGE,"E67"),sQuery(id+"F0.wireOp",EDGE,"E68")])],"isStart":true}),makeQuery(id+"F3.opExtrude","CAP_FACE",FACE,{"disambiguationData":[OSD([sQuery(id+"F2.wireOp",EDGE,"E90"),sQuery(id+"F2.wireOp",EDGE,"E91.0"),sQuery(id+"F2.wireOp",EDGE,"E91.1"),sQuery(id+"F2.wireOp",EDGE,"E91.2"),sQuery(id+"F2.wireOp",EDGE,"E91.3"),sQuery(id+"F2.wireOp",EDGE,"E91.4"),sQuery(id+"F2.wireOp",EDGE,"E91.5")])],"isStart":true})]}),makeQuery(id+"F6.opExtrude","SWEPT_FACE",FACE,{"disambiguationData":[OSD([sQuery(id+"F5.wireOp",EDGE,"E92.top")])]})]});
            var Q66;
            Q66=makeQuery(id+"F6.boolean.opBoolean","INTERSECT",EDGE,{"derivedFrom":[makeQuery(id+"F3.boolean.opBoolean","MERGE",FACE,{"derivedFrom":[makeQuery(id+"F1.opExtrude","CAP_FACE",FACE,{"disambiguationData":[OSD([sQuery(id+"F0.wireOp",EDGE,"E3.0"),sQuery(id+"F0.wireOp",EDGE,"E3.1"),sQuery(id+"F0.wireOp",EDGE,"E3.2"),sQuery(id+"F0.wireOp",EDGE,"E3.3"),sQuery(id+"F0.wireOp",EDGE,"E3.4"),sQuery(id+"F0.wireOp",EDGE,"E3.5"),sQuery(id+"F0.wireOp",EDGE,"E4.0"),sQuery(id+"F0.wireOp",EDGE,"E4.1"),sQuery(id+"F0.wireOp",EDGE,"E4.2"),sQuery(id+"F0.wireOp",EDGE,"E4.3"),sQuery(id+"F0.wireOp",EDGE,"E4.4"),sQuery(id+"F0.wireOp",EDGE,"E4.5"),sQuery(id+"F0.wireOp",EDGE,"E5.0"),sQuery(id+"F0.wireOp",EDGE,"E5.1"),sQuery(id+"F0.wireOp",EDGE,"E5.2"),sQuery(id+"F0.wireOp",EDGE,"E5.3"),sQuery(id+"F0.wireOp",EDGE,"E5.4"),sQuery(id+"F0.wireOp",EDGE,"E5.5"),sQuery(id+"F0.wireOp",EDGE,"E6.0"),sQuery(id+"F0.wireOp",EDGE,"E6.1"),sQuery(id+"F0.wireOp",EDGE,"E6.2"),sQuery(id+"F0.wireOp",EDGE,"E6.3"),sQuery(id+"F0.wireOp",EDGE,"E6.4"),sQuery(id+"F0.wireOp",EDGE,"E6.5"),sQuery(id+"F0.wireOp",EDGE,"E7.0"),sQuery(id+"F0.wireOp",EDGE,"E7.1"),sQuery(id+"F0.wireOp",EDGE,"E7.2"),sQuery(id+"F0.wireOp",EDGE,"E7.3"),sQuery(id+"F0.wireOp",EDGE,"E7.4"),sQuery(id+"F0.wireOp",EDGE,"E7.5"),sQuery(id+"F0.wireOp",EDGE,"E8.0"),sQuery(id+"F0.wireOp",EDGE,"E8.1"),sQuery(id+"F0.wireOp",EDGE,"E8.2"),sQuery(id+"F0.wireOp",EDGE,"E8.3"),sQuery(id+"F0.wireOp",EDGE,"E8.4"),sQuery(id+"F0.wireOp",EDGE,"E8.5"),sQuery(id+"F0.wireOp",EDGE,"E9.0"),sQuery(id+"F0.wireOp",EDGE,"E9.1"),sQuery(id+"F0.wireOp",EDGE,"E9.5"),sQuery(id+"F0.wireOp",EDGE,"E10.0"),sQuery(id+"F0.wireOp",EDGE,"E10.1"),sQuery(id+"F0.wireOp",EDGE,"E10.5"),sQuery(id+"F0.wireOp",EDGE,"E11.0"),sQuery(id+"F0.wireOp",EDGE,"E11.1"),sQuery(id+"F0.wireOp",EDGE,"E11.5"),sQuery(id+"F0.wireOp",EDGE,"E12.0"),sQuery(id+"F0.wireOp",EDGE,"E12.1"),sQuery(id+"F0.wireOp",EDGE,"E12.5"),sQuery(id+"F0.wireOp",EDGE,"E13.0"),sQuery(id+"F0.wireOp",EDGE,"E13.1"),sQuery(id+"F0.wireOp",EDGE,"E13.5"),sQuery(id+"F0.wireOp",EDGE,"E14.0"),sQuery(id+"F0.wireOp",EDGE,"E14.1"),sQuery(id+"F0.wireOp",EDGE,"E14.2"),sQuery(id+"F0.wireOp",EDGE,"E14.3"),sQuery(id+"F0.wireOp",EDGE,"E14.5"),sQuery(id+"F0.wireOp",EDGE,"E15"),sQuery(id+"F0.wireOp",EDGE,"E17"),sQuery(id+"F0.wireOp",EDGE,"E18"),sQuery(id+"F0.wireOp",EDGE,"E21"),sQuery(id+"F0.wireOp",EDGE,"E23"),sQuery(id+"F0.wireOp",EDGE,"E24"),sQuery(id+"F0.wireOp",EDGE,"E26"),sQuery(id+"F0.wireOp",EDGE,"E29"),sQuery(id+"F0.wireOp",EDGE,"E30"),sQuery(id+"F0.wireOp",EDGE,"E32"),sQuery(id+"F0.wireOp",EDGE,"E33.top"),sQuery(id+"F0.wireOp",EDGE,"E34.top"),sQuery(id+"F0.wireOp",EDGE,"E40"),sQuery(id+"F0.wireOp",EDGE,"E46"),sQuery(id+"F0.wireOp",EDGE,"E35"),sQuery(id+"F0.wireOp",EDGE,"E52"),sQuery(id+"F0.wireOp",EDGE,"E1.1"),sQuery(id+"F0.wireOp",EDGE,"E1.2"),sQuery(id+"F0.wireOp",EDGE,"E1.4"),sQuery(id+"F0.wireOp",EDGE,"E1.5"),sQuery(id+"F0.wireOp",EDGE,"E56"),sQuery(id+"F0.wireOp",EDGE,"E57"),sQuery(id+"F0.wireOp",EDGE,"E58"),sQuery(id+"F0.wireOp",EDGE,"E59"),sQuery(id+"F0.wireOp",EDGE,"E60"),sQuery(id+"F0.wireOp",EDGE,"E61"),sQuery(id+"F0.wireOp",EDGE,"E62"),sQuery(id+"F0.wireOp",EDGE,"E63"),sQuery(id+"F0.wireOp",EDGE,"E64"),sQuery(id+"F0.wireOp",EDGE,"E65"),sQuery(id+"F0.wireOp",EDGE,"E66"),sQuery(id+"F0.wireOp",EDGE,"E67"),sQuery(id+"F0.wireOp",EDGE,"E68")])],"isStart":true}),makeQuery(id+"F3.opExtrude","CAP_FACE",FACE,{"disambiguationData":[OSD([sQuery(id+"F2.wireOp",EDGE,"E90"),sQuery(id+"F2.wireOp",EDGE,"E91.0"),sQuery(id+"F2.wireOp",EDGE,"E91.1"),sQuery(id+"F2.wireOp",EDGE,"E91.2"),sQuery(id+"F2.wireOp",EDGE,"E91.3"),sQuery(id+"F2.wireOp",EDGE,"E91.4"),sQuery(id+"F2.wireOp",EDGE,"E91.5")])],"isStart":true})]}),makeQuery(id+"F6.opExtrude","SWEPT_FACE",FACE,{"disambiguationData":[OSD([sQuery(id+"F5.wireOp",EDGE,"E92.left")])]})]});
            var Q67;
            Q67=makeQuery(id+"F3.opExtrude","CAP_EDGE",EDGE,{"disambiguationData":[OSD([sQuery(id+"F2.wireOp",EDGE,"E91.3")])],"isStart":true});
            var Q68;
            Q68=makeQuery(id+"F1.opExtrude","CAP_EDGE",EDGE,{"disambiguationData":[OSD([sQuery(id+"F0.wireOp",EDGE,"E13.0"),sQuery(id+"F0.wireOp",EDGE,"E33.top")])],"isStart":true});
            var Q69;
            Q69=makeQuery(id+"F1.opExtrude","CAP_EDGE",EDGE,{"disambiguationData":[OSD([sQuery(id+"F0.wireOp",EDGE,"E14.0")])],"isStart":true});
            var Q70;
            Q70=makeQuery(id+"F1.opExtrude","CAP_EDGE",EDGE,{"disambiguationData":[OSD([sQuery(id+"F0.wireOp",EDGE,"E52")])],"isStart":true});
            var Q71;
            Q71=makeQuery(id+"F1.opExtrude","CAP_EDGE",EDGE,{"disambiguationData":[OSD([sQuery(id+"F0.wireOp",EDGE,"E40")])],"isStart":true});
            var Q72;
            Q72=makeQuery(id+"F3.opExtrude","CAP_EDGE",EDGE,{"disambiguationData":[OSD([sQuery(id+"F2.wireOp",EDGE,"E91.2")])],"isStart":true});
            var Q73;
            Q73=makeQuery(id+"F3.opExtrude","CAP_EDGE",EDGE,{"disambiguationData":[OSD([sQuery(id+"F2.wireOp",EDGE,"E91.4")])],"isStart":true});
            var Q74;
            Q74=makeQuery(id+"F1.opExtrude","CAP_EDGE",EDGE,{"disambiguationData":[OSD([sQuery(id+"F0.wireOp",EDGE,"E12.0")])],"isStart":true});
            var Q75;
            {var subQ0=sQuery(id+"F0.wireOp",EDGE,"E12.5");Q75=makeQuery(id+"F1.opExtrude","CAP_EDGE",EDGE,{"disambiguationData":[OSD([subQ0]),TDD([makeQuery(id+"F0.imprint","IMPRINT",EDGE,{"disambiguationData":[TD([[makeQuery(id+"F0.imprint","INTERSECT",VERTEX,{"derivedFrom":[sQuery(id+"F0.wireOp",EDGE,"E12.0"),subQ0]}),1.0]])],"derivedFrom":subQ0})])],"isStart":true});}
            chamfer(context, id + "F7", {"entities" : qUnion([Q0, Q1, Q2, Q3, Q4, Q5, Q6, Q7, Q8, Q9, Q10, Q11, Q12, Q13, Q14, Q15, Q16, Q17, Q18, Q19, Q20, Q21, Q22, Q23, Q24, Q25, Q26, Q27, Q28, Q29, Q30, Q31, Q32, Q33, Q34, Q35, Q36, Q37, Q38, Q39, Q40, Q41, Q42, Q43, Q44, Q45, Q46, Q47, Q48, Q49, Q50, Q51, Q52, Q53, Q54, Q55, Q56, Q57, Q58, Q59, Q60, Q61, Q62, Q63, Q64, Q65, Q66, Q67, Q68, Q69, Q70, Q71, Q72, Q73, Q74, Q75]), "width" : 0.76 * mm, "tangentPropagation" : true});
        }
    });
